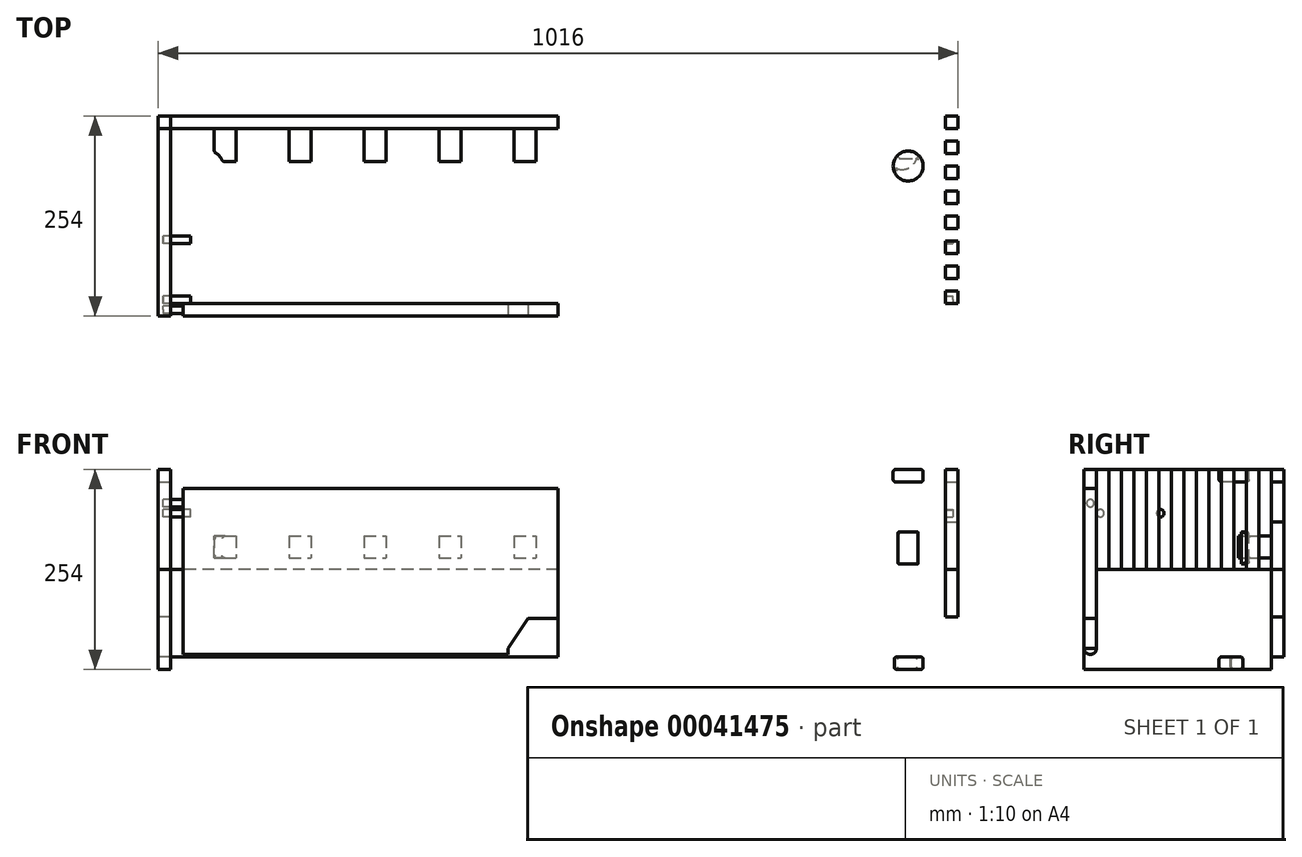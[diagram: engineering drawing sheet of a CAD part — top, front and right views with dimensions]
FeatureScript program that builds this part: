
annotation { "Feature Type Name" : "Feature", "Feature Type Description" : "" }
export const myFeature = defineFeature(function(context is Context, id is Id, definition is map)
    precondition{}
    {
        {
            var Q0;
            Q0=qCreatedBy(makeId("Top.planeOp"),FACE);
            var sketch = newSketch(context, id + "F0", { "sketchPlane" : qUnion([Q0])});
            skLineSegment(sketch, "E0.bottom", {"start": v(-508, 127) * mm, "end": v(0, 127) * mm});
            skLineSegment(sketch, "E0.top", {"start": v(-508, -127) * mm, "end": v(0, -127) * mm});
            skLineSegment(sketch, "E0.left", {"start": v(-508, 127) * mm, "end": v(-508, -127) * mm});
            skLineSegment(sketch, "E0.right", {"start": v(0, 127) * mm, "end": v(0, -127) * mm});
            skLineSegment(sketch, "E1.bottom", {"start": v(-508, 127) * mm, "end": v(-492.13, 127) * mm});
            skLineSegment(sketch, "E1.top", {"start": v(-508, 111.12) * mm, "end": v(-492.13, 111.12) * mm});
            skLineSegment(sketch, "E1.left", {"start": v(-508, 127) * mm, "end": v(-508, 111.12) * mm});
            skLineSegment(sketch, "E1.right", {"start": v(-492.13, 127) * mm, "end": v(-492.13, 111.12) * mm});
            skLineSegment(sketch, "E2.0.1.0", {"start": v(-508, 95.25) * mm, "end": v(-508, 79.37) * mm});
            skLineSegment(sketch, "E2.0.1.1", {"start": v(-508, 95.25) * mm, "end": v(-492.13, 95.25) * mm});
            skLineSegment(sketch, "E2.0.1.2", {"start": v(-492.13, 95.25) * mm, "end": v(-492.13, 79.37) * mm});
            skLineSegment(sketch, "E2.0.1.3", {"start": v(-508, 79.37) * mm, "end": v(-492.13, 79.37) * mm});
            skLineSegment(sketch, "E2.0.2.0", {"start": v(-508, 63.5) * mm, "end": v(-508, 47.62) * mm});
            skLineSegment(sketch, "E2.0.2.1", {"start": v(-508, 63.5) * mm, "end": v(-492.13, 63.5) * mm});
            skLineSegment(sketch, "E2.0.2.2", {"start": v(-492.13, 63.5) * mm, "end": v(-492.13, 47.62) * mm});
            skLineSegment(sketch, "E2.0.2.3", {"start": v(-508, 47.62) * mm, "end": v(-492.13, 47.62) * mm});
            skLineSegment(sketch, "E2.0.3.0", {"start": v(-508, 31.75) * mm, "end": v(-508, 15.87) * mm});
            skLineSegment(sketch, "E2.0.3.1", {"start": v(-508, 31.75) * mm, "end": v(-492.13, 31.75) * mm});
            skLineSegment(sketch, "E2.0.3.2", {"start": v(-492.13, 31.75) * mm, "end": v(-492.13, 15.88) * mm});
            skLineSegment(sketch, "E2.0.3.3", {"start": v(-508, 15.87) * mm, "end": v(-492.13, 15.87) * mm});
            skLineSegment(sketch, "E2.0.4.0", {"start": v(-508, 0) * mm, "end": v(-508, -15.88) * mm});
            skLineSegment(sketch, "E2.0.4.1", {"start": v(-508, 0) * mm, "end": v(-492.13, 0) * mm});
            skLineSegment(sketch, "E2.0.4.2", {"start": v(-492.13, 0) * mm, "end": v(-492.13, -15.87) * mm});
            skLineSegment(sketch, "E2.0.4.3", {"start": v(-508, -15.88) * mm, "end": v(-492.13, -15.88) * mm});
            skLineSegment(sketch, "E2.0.5.0", {"start": v(-508, -31.75) * mm, "end": v(-508, -47.62) * mm});
            skLineSegment(sketch, "E2.0.5.1", {"start": v(-508, -31.75) * mm, "end": v(-492.13, -31.75) * mm});
            skLineSegment(sketch, "E2.0.5.2", {"start": v(-492.13, -31.75) * mm, "end": v(-492.13, -47.62) * mm});
            skLineSegment(sketch, "E2.0.5.3", {"start": v(-508, -47.63) * mm, "end": v(-492.13, -47.63) * mm});
            skLineSegment(sketch, "E2.0.6.0", {"start": v(-508, -63.5) * mm, "end": v(-508, -79.37) * mm});
            skLineSegment(sketch, "E2.0.6.1", {"start": v(-508, -63.5) * mm, "end": v(-492.13, -63.5) * mm});
            skLineSegment(sketch, "E2.0.6.2", {"start": v(-492.13, -63.5) * mm, "end": v(-492.13, -79.37) * mm});
            skLineSegment(sketch, "E2.0.6.3", {"start": v(-508, -79.38) * mm, "end": v(-492.13, -79.38) * mm});
            skLineSegment(sketch, "E2.0.7.0", {"start": v(-508, -95.25) * mm, "end": v(-508, -111.12) * mm});
            skLineSegment(sketch, "E2.0.7.1", {"start": v(-508, -95.25) * mm, "end": v(-492.13, -95.25) * mm});
            skLineSegment(sketch, "E2.0.7.2", {"start": v(-492.13, -95.25) * mm, "end": v(-492.13, -111.12) * mm});
            skLineSegment(sketch, "E2.0.7.3", {"start": v(-508, -111.13) * mm, "end": v(-492.13, -111.13) * mm});
            skLineSegment(sketch, "E2.direction1", {"start": v(-508, 111.12) * mm, "end": v(-482.6, 111.12) * mm, "construction": true});
            skLineSegment(sketch, "E2.direction2", {"start": v(-508, 111.12) * mm, "end": v(-508, 79.37) * mm, "construction": true});
            skLineSegment(sketch, "E3.MirrorCS", {"start": v(508, 127) * mm, "end": v(508, 111.13) * mm});
            skLineSegment(sketch, "E4.MirrorCS", {"start": v(508, 111.13) * mm, "end": v(492.12, 111.13) * mm});
            skLineSegment(sketch, "E5.MirrorCS", {"start": v(508, 111.13) * mm, "end": v(482.6, 111.13) * mm});
            skLineSegment(sketch, "E6.MirrorCS", {"start": v(508, 111.13) * mm, "end": v(508, 79.38) * mm});
            skLineSegment(sketch, "E7.MirrorCS", {"start": v(492.13, -31.75) * mm, "end": v(492.13, -47.62) * mm});
            skLineSegment(sketch, "E8.MirrorCS", {"start": v(508, 15.88) * mm, "end": v(492.13, 15.88) * mm});
            skLineSegment(sketch, "E9.MirrorCS", {"start": v(508, 127) * mm, "end": v(492.12, 127) * mm});
            skLineSegment(sketch, "E10.MirrorCS", {"start": v(508, 63.5) * mm, "end": v(492.12, 63.5) * mm});
            skLineSegment(sketch, "E11.MirrorCS", {"start": v(492.12, 63.5) * mm, "end": v(492.12, 47.63) * mm});
            skLineSegment(sketch, "E12.MirrorCS", {"start": v(492.12, 127) * mm, "end": v(492.12, 111.13) * mm});
            skLineSegment(sketch, "E13.MirrorCS", {"start": v(508, 95.25) * mm, "end": v(508, 79.38) * mm});
            skLineSegment(sketch, "E14.MirrorCS", {"start": v(508, 95.25) * mm, "end": v(492.12, 95.25) * mm});
            skLineSegment(sketch, "E15.MirrorCS", {"start": v(492.12, 95.25) * mm, "end": v(492.12, 79.38) * mm});
            skLineSegment(sketch, "E16.MirrorCS", {"start": v(508, 79.38) * mm, "end": v(492.12, 79.38) * mm});
            skLineSegment(sketch, "E17.MirrorCS", {"start": v(508, 63.5) * mm, "end": v(508, 47.63) * mm});
            skLineSegment(sketch, "E18.MirrorCS", {"start": v(508, -47.62) * mm, "end": v(492.13, -47.62) * mm});
            skLineSegment(sketch, "E19.MirrorCS", {"start": v(508, -15.87) * mm, "end": v(492.13, -15.87) * mm});
            skLineSegment(sketch, "E20.MirrorCS", {"start": v(508, 0) * mm, "end": v(508, -15.87) * mm});
            skLineSegment(sketch, "E21.MirrorCS", {"start": v(508, -63.5) * mm, "end": v(492.13, -63.5) * mm});
            skLineSegment(sketch, "E22.MirrorCS", {"start": v(508, 31.75) * mm, "end": v(508, 15.88) * mm});
            skLineSegment(sketch, "E23.MirrorCS", {"start": v(508, -95.25) * mm, "end": v(508, -111.12) * mm});
            skLineSegment(sketch, "E24.MirrorCS", {"start": v(492.13, -95.25) * mm, "end": v(492.13, -111.12) * mm});
            skLineSegment(sketch, "E25.MirrorCS", {"start": v(508, 0) * mm, "end": v(492.13, 0) * mm});
            skLineSegment(sketch, "E26.MirrorCS", {"start": v(492.13, -63.5) * mm, "end": v(492.13, -79.37) * mm});
            skLineSegment(sketch, "E27.MirrorCS", {"start": v(508, 31.75) * mm, "end": v(492.13, 31.75) * mm});
            skLineSegment(sketch, "E28.MirrorCS", {"start": v(508, -95.25) * mm, "end": v(492.13, -95.25) * mm});
            skLineSegment(sketch, "E29.MirrorCS", {"start": v(508, -31.75) * mm, "end": v(492.13, -31.75) * mm});
            skLineSegment(sketch, "E30.MirrorCS", {"start": v(492.13, 0) * mm, "end": v(492.13, -15.87) * mm});
            skLineSegment(sketch, "E31.MirrorCS", {"start": v(508, -79.37) * mm, "end": v(492.13, -79.37) * mm});
            skLineSegment(sketch, "E32.MirrorCS", {"start": v(492.13, 31.75) * mm, "end": v(492.13, 15.88) * mm});
            skLineSegment(sketch, "E33.MirrorCS", {"start": v(508, -111.12) * mm, "end": v(492.13, -111.12) * mm});
            skLineSegment(sketch, "E34.MirrorCS", {"start": v(508, 127) * mm, "end": v(508, -127) * mm});
            skLineSegment(sketch, "E35.MirrorCS", {"start": v(508, 47.63) * mm, "end": v(492.13, 47.63) * mm});
            skLineSegment(sketch, "E36.MirrorCS", {"start": v(508, -63.5) * mm, "end": v(508, -79.37) * mm});
            skLineSegment(sketch, "E37.MirrorCS", {"start": v(508, -31.75) * mm, "end": v(508, -47.62) * mm});
            skLineSegment(sketch, "E38.MirrorCS", {"start": v(508, 127) * mm, "end": v(0, 127) * mm});
            skLineSegment(sketch, "E39.MirrorCS", {"start": v(508, -127) * mm, "end": v(0, -127) * mm});
            skSolve(sketch);
        }
        {
            var Q0;
            Q0=makeQuery(id+"F0.imprint","IMPRINT",FACE,{"disambiguationData":[TD([[makeQuery(id+"F0.imprint","IMPRINT",EDGE,{"derivedFrom":sQuery(id+"F0.wireOp",EDGE,"E0.bottom")}),-1.0]])]});
            var Q1;
            {var subQ2=sQuery(id+"F0.wireOp",EDGE,"E0.right");Q1=makeQuery(id+"F0.imprint","IMPRINT",FACE,{"disambiguationData":[TD([[makeQuery(id+"F0.imprint","IMPRINT",EDGE,{"derivedFrom":subQ2}),1.0]])]});}
            extrude(context, id + "F1", {"entities" : qUnion([Q0, Q1]), "oppositeDirection" : true, "depth" : 15.88 * mm});
        }
        {
            var Q0;
            {var subQ0=sQuery(id+"F0.wireOp",EDGE,"E0.left");Q0=makeQuery(id+"F1.opExtrude","SWEPT_FACE",FACE,{"disambiguationData":[OSD([subQ0]),TDD([makeQuery(id+"F0.imprint","IMPRINT",EDGE,{"disambiguationData":[TD([[makeQuery(id+"F0.imprint","INTERSECT",VERTEX,{"derivedFrom":[subQ0,sQuery(id+"F0.wireOp",EDGE,"E1.top"),sQuery(id+"F0.wireOp",EDGE,"E1.left")]}),-1.0]])],"derivedFrom":subQ0})])]});}
            var sketch = newSketch(context, id + "F2", { "sketchPlane" : qUnion([Q0])});
            skLineSegment(sketch, "E40.bottom", {"start": v(-127, 0) * mm, "end": v(127, 0) * mm});
            skLineSegment(sketch, "E40.top", {"start": v(-127, -127) * mm, "end": v(127, -127) * mm});
            skLineSegment(sketch, "E40.left", {"start": v(-127, 0) * mm, "end": v(-127, -127) * mm});
            skLineSegment(sketch, "E40.right", {"start": v(127, 0) * mm, "end": v(127, -127) * mm});
            skSolve(sketch);
        }
        {
            var Q0;
            Q0=makeQuery(id+"F2.imprint","IMPRINT",FACE,{"disambiguationData":[TD([[makeQuery(id+"F2.imprint","IMPRINT",EDGE,{"derivedFrom":sQuery(id+"F2.wireOp",EDGE,"E40.top")}),1.0]])]});
            extrude(context, id + "F3", {"entities" : qUnion([Q0]), "oppositeDirection" : true, "depth" : 15.88 * mm});
        }
        {
            var Q0;
            Q0=makeQuery(id+"F1.opExtrude","SWEPT_BODY",BODY,{"disambiguationData":[OSD([sQuery(id+"F0.wireOp",EDGE,"E0.bottom"),sQuery(id+"F0.wireOp",EDGE,"E0.top"),sQuery(id+"F0.wireOp",EDGE,"E0.left"),sQuery(id+"F0.wireOp",EDGE,"E1.top"),sQuery(id+"F0.wireOp",EDGE,"E1.right"),sQuery(id+"F0.wireOp",EDGE,"E2.0.1.1"),sQuery(id+"F0.wireOp",EDGE,"E2.0.1.2"),sQuery(id+"F0.wireOp",EDGE,"E2.0.1.3"),sQuery(id+"F0.wireOp",EDGE,"E2.0.2.1"),sQuery(id+"F0.wireOp",EDGE,"E2.0.2.2"),sQuery(id+"F0.wireOp",EDGE,"E2.0.2.3"),sQuery(id+"F0.wireOp",EDGE,"E2.0.3.1"),sQuery(id+"F0.wireOp",EDGE,"E2.0.3.2"),sQuery(id+"F0.wireOp",EDGE,"E2.0.3.3"),sQuery(id+"F0.wireOp",EDGE,"E2.0.4.1"),sQuery(id+"F0.wireOp",EDGE,"E2.0.4.2"),sQuery(id+"F0.wireOp",EDGE,"E2.0.4.3"),sQuery(id+"F0.wireOp",EDGE,"E2.0.5.1"),sQuery(id+"F0.wireOp",EDGE,"E2.0.5.2"),sQuery(id+"F0.wireOp",EDGE,"E2.0.5.3"),sQuery(id+"F0.wireOp",EDGE,"E2.0.6.1"),sQuery(id+"F0.wireOp",EDGE,"E2.0.6.2"),sQuery(id+"F0.wireOp",EDGE,"E2.0.6.3"),sQuery(id+"F0.wireOp",EDGE,"E2.0.7.1"),sQuery(id+"F0.wireOp",EDGE,"E2.0.7.2"),sQuery(id+"F0.wireOp",EDGE,"E2.0.7.3"),sQuery(id+"F0.wireOp",EDGE,"E5.MirrorCS"),sQuery(id+"F0.wireOp",EDGE,"E7.MirrorCS"),sQuery(id+"F0.wireOp",EDGE,"E8.MirrorCS"),sQuery(id+"F0.wireOp",EDGE,"E10.MirrorCS"),sQuery(id+"F0.wireOp",EDGE,"E11.MirrorCS"),sQuery(id+"F0.wireOp",EDGE,"E12.MirrorCS"),sQuery(id+"F0.wireOp",EDGE,"E14.MirrorCS"),sQuery(id+"F0.wireOp",EDGE,"E15.MirrorCS"),sQuery(id+"F0.wireOp",EDGE,"E16.MirrorCS"),sQuery(id+"F0.wireOp",EDGE,"E18.MirrorCS"),sQuery(id+"F0.wireOp",EDGE,"E19.MirrorCS"),sQuery(id+"F0.wireOp",EDGE,"E21.MirrorCS"),sQuery(id+"F0.wireOp",EDGE,"E24.MirrorCS"),sQuery(id+"F0.wireOp",EDGE,"E25.MirrorCS"),sQuery(id+"F0.wireOp",EDGE,"E26.MirrorCS"),sQuery(id+"F0.wireOp",EDGE,"E27.MirrorCS"),sQuery(id+"F0.wireOp",EDGE,"E28.MirrorCS"),sQuery(id+"F0.wireOp",EDGE,"E29.MirrorCS"),sQuery(id+"F0.wireOp",EDGE,"E30.MirrorCS"),sQuery(id+"F0.wireOp",EDGE,"E31.MirrorCS"),sQuery(id+"F0.wireOp",EDGE,"E32.MirrorCS"),sQuery(id+"F0.wireOp",EDGE,"E33.MirrorCS"),sQuery(id+"F0.wireOp",EDGE,"E34.MirrorCS"),sQuery(id+"F0.wireOp",EDGE,"E35.MirrorCS"),sQuery(id+"F0.wireOp",EDGE,"E38.MirrorCS"),sQuery(id+"F0.wireOp",EDGE,"E39.MirrorCS")])]});
            var Q1;
            Q1=makeQuery(id+"F3.opExtrude","SWEPT_BODY",BODY,{"disambiguationData":[OSD([sQuery(id+"F0.wireOp",EDGE,"E0.left"),sQuery(id+"F0.wireOp",EDGE,"E1.top"),sQuery(id+"F0.wireOp",EDGE,"E1.left"),sQuery(id+"F0.wireOp",EDGE,"E2.0.1.0"),sQuery(id+"F0.wireOp",EDGE,"E2.0.1.1"),sQuery(id+"F2.wireOp",EDGE,"E40.bottom"),sQuery(id+"F2.wireOp",EDGE,"E40.top"),sQuery(id+"F2.wireOp",EDGE,"E40.left"),sQuery(id+"F2.wireOp",EDGE,"E40.right")])]});
            booleanBodies(context, id + "F4", {"operationType" : BooleanOperationType.SUBTRACTION, "tools" : qUnion([Q0]), "targets" : qUnion([Q1]), "keepTools" : true});
        }
        {
            var Q0;
            Q0=makeQuery(id+"F3.opExtrude","SWEPT_FACE",FACE,{"disambiguationData":[OSD([sQuery(id+"F2.wireOp",EDGE,"E40.top")])]});
            cPlane(context, id + "F5", {"entities" : qUnion([Q0]), "cplaneType" : CPlaneType.OFFSET, "offset" : 0 * mm, "width" : 152.4 * mm, "height" : 152.4 * mm});
        }
        {
            var Q0;
            Q0=makeQuery(id+"F3.opExtrude","SWEPT_BODY",BODY,{"disambiguationData":[OSD([sQuery(id+"F0.wireOp",EDGE,"E0.left"),sQuery(id+"F0.wireOp",EDGE,"E1.top"),sQuery(id+"F0.wireOp",EDGE,"E1.left"),sQuery(id+"F0.wireOp",EDGE,"E2.0.1.0"),sQuery(id+"F0.wireOp",EDGE,"E2.0.1.1"),sQuery(id+"F2.wireOp",EDGE,"E40.bottom"),sQuery(id+"F2.wireOp",EDGE,"E40.top"),sQuery(id+"F2.wireOp",EDGE,"E40.left"),sQuery(id+"F2.wireOp",EDGE,"E40.right")])]});
            var Q1;
            Q1=qCreatedBy(id+"F5.planeOp",FACE);
            mirror(context, id + "F6", {"entities" : qUnion([Q0]), "mirrorPlane" : qUnion([Q1])});
        }
        {
            var Q0;
            Q0=makeQuery(id+"F3.opExtrude","CAP_FACE",FACE,{"disambiguationData":[OSD([sQuery(id+"F0.wireOp",EDGE,"E0.left"),sQuery(id+"F0.wireOp",EDGE,"E1.top"),sQuery(id+"F0.wireOp",EDGE,"E1.left"),sQuery(id+"F0.wireOp",EDGE,"E2.0.1.0"),sQuery(id+"F0.wireOp",EDGE,"E2.0.1.1"),sQuery(id+"F2.wireOp",EDGE,"E40.bottom"),sQuery(id+"F2.wireOp",EDGE,"E40.top"),sQuery(id+"F2.wireOp",EDGE,"E40.left"),sQuery(id+"F2.wireOp",EDGE,"E40.right")])],"isStart":false});
            var sketch = newSketch(context, id + "F7", { "sketchPlane" : qUnion([Q0])});
            skLineSegment(sketch, "E41.bottom", {"start": v(-127, -23.81) * mm, "end": v(-111.12, -23.81) * mm});
            skLineSegment(sketch, "E41.top", {"start": v(-118.77, -234.95) * mm, "end": v(-118.77, -234.95) * mm});
            skLineSegment(sketch, "E41.left", {"start": v(-127, -23.81) * mm, "end": v(-127, -227.01) * mm});
            skLineSegment(sketch, "E41.right", {"start": v(-111.12, -23.81) * mm, "end": v(-111.12, -227.01) * mm});
            skCircle(sketch, "E42", {"center": v(-119.06, -42.86) * mm, "radius": 20.64 * mm, "construction": true});
            skPoint(sketch, "E42.centerSnap0", {"position": v(-119.06, -23.81) * mm});
            skPoint(sketch, "E43", {"position": v(-119.06, -22.23) * mm});
            skCircle(sketch, "E44", {"center": v(-119.06, -42.86) * mm, "radius": 7.94 * mm, "construction": true});
            skPoint(sketch, "E45", {"position": v(-119.06, -50.8) * mm});
            skLineSegment(sketch, "E46", {"start": v(-119.06, -50.8) * mm, "end": v(-30.16, -50.8) * mm, "construction": true});
            skPoint(sketch, "E47", {"position": v(-30.16, -55.56) * mm});
            skCircle(sketch, "E48", {"center": v(-119.06, -42.86) * mm, "radius": 4.76 * mm});
            skCircle(sketch, "E49", {"center": v(-30.16, -55.56) * mm, "radius": 4.76 * mm});
            skPoint(sketch, "E50", {"position": v(-106.36, -55.56) * mm});
            skCircle(sketch, "E51", {"center": v(-106.36, -55.56) * mm, "radius": 4.76 * mm});
            skPoint(sketch, "E52.visualSharp", {"position": v(-127, -234.95) * mm});
            skArc(sketch, "E52.filletArc", {"start": v(-127, -227.01) * mm, "mid": v(-124.68, -232.63) * mm, "end": v(-119.06, -234.95) * mm});
            skPoint(sketch, "E53.visualSharp", {"position": v(-111.12, -234.95) * mm});
            skArc(sketch, "E53.filletArc", {"start": v(-119.06, -234.95) * mm, "mid": v(-113.45, -232.63) * mm, "end": v(-111.12, -227.01) * mm});
            skLineSegment(sketch, "E54.bottom", {"start": v(-123.82, -42.86) * mm, "end": v(-114.3, -42.86) * mm});
            skLineSegment(sketch, "E54.top", {"start": v(-123.82, -195.26) * mm, "end": v(-114.3, -195.26) * mm});
            skLineSegment(sketch, "E54.left", {"start": v(-123.82, -42.86) * mm, "end": v(-123.82, -195.26) * mm});
            skLineSegment(sketch, "E54.right", {"start": v(-114.3, -42.86) * mm, "end": v(-114.3, -195.26) * mm});
            skSolve(sketch);
        }
        {
            var Q0;
            Q0=makeQuery(id+"F7.imprint","IMPRINT",FACE,{"disambiguationData":[TD([[makeQuery(id+"F7.imprint","IMPRINT",EDGE,{"derivedFrom":sQuery(id+"F7.wireOp",EDGE,"E51")}),1.0]])]});
            var Q1;
            Q1=makeQuery(id+"F7.imprint","IMPRINT",FACE,{"disambiguationData":[TD([[makeQuery(id+"F7.imprint","IMPRINT",EDGE,{"derivedFrom":sQuery(id+"F7.wireOp",EDGE,"E48")}),1.0]])]});
            var Q2;
            Q2=makeQuery(id+"F7.imprint","IMPRINT",FACE,{"disambiguationData":[TD([[makeQuery(id+"F7.imprint","IMPRINT",EDGE,{"derivedFrom":sQuery(id+"F7.wireOp",EDGE,"E49")}),1.0]])]});
            extrude(context, id + "F8", {"entities" : qUnion([Q0, Q1, Q2]), "depth" : 25.4 * mm, "hasSecondDirection" : true, "secondDirectionOppositeDirection" : true, "secondDirectionDepth" : 9.52 * mm});
        }
        {
            var Q0;
            Q0=makeQuery(id+"F1.opExtrude","SWEPT_FACE",FACE,{"disambiguationData":[OSD([sQuery(id+"F0.wireOp",EDGE,"E0.bottom"),sQuery(id+"F0.wireOp",EDGE,"E38.MirrorCS")])]});
            var sketch = newSketch(context, id + "F9", { "sketchPlane" : qUnion([Q0])});
            skLineSegment(sketch, "E55", {"start": v(0, -15.88) * mm, "end": v(492.13, -15.88) * mm});
            skLineSegment(sketch, "E56", {"start": v(492.13, -15.88) * mm, "end": v(492.13, -66.67) * mm});
            skLineSegment(sketch, "E57", {"start": v(492.12, -66.68) * mm, "end": v(508, -66.68) * mm});
            skLineSegment(sketch, "E58", {"start": v(508, -66.68) * mm, "end": v(508, -127) * mm});
            skLineSegment(sketch, "E59", {"start": v(0, -15.88) * mm, "end": v(0, -127) * mm});
            skLineSegment(sketch, "E60", {"start": v(0, -127) * mm, "end": v(508, -127) * mm});
            skLineSegment(sketch, "E61.MirrorCS", {"start": v(0, -238.13) * mm, "end": v(0, -127) * mm});
            skLineSegment(sketch, "E62.MirrorCS", {"start": v(0, -238.13) * mm, "end": v(492.13, -238.13) * mm});
            skLineSegment(sketch, "E63.MirrorCS", {"start": v(492.13, -238.13) * mm, "end": v(492.13, -187.33) * mm});
            skLineSegment(sketch, "E64.MirrorCS", {"start": v(492.12, -187.33) * mm, "end": v(508, -187.33) * mm});
            skLineSegment(sketch, "E65.MirrorCS", {"start": v(508, -187.33) * mm, "end": v(508, -127) * mm});
            skLineSegment(sketch, "E66.MirrorCS", {"start": v(0, -15.88) * mm, "end": v(-492.13, -15.88) * mm});
            skLineSegment(sketch, "E67.MirrorCS", {"start": v(-492.13, -15.88) * mm, "end": v(-492.13, -66.67) * mm});
            skLineSegment(sketch, "E68.MirrorCS", {"start": v(-492.12, -187.33) * mm, "end": v(-508, -187.33) * mm});
            skLineSegment(sketch, "E69.MirrorCS", {"start": v(-492.12, -66.68) * mm, "end": v(-508, -66.68) * mm});
            skLineSegment(sketch, "E70.MirrorCS", {"start": v(-508, -187.33) * mm, "end": v(-508, -127) * mm});
            skLineSegment(sketch, "E71.MirrorCS", {"start": v(-508, -66.67) * mm, "end": v(-508, -127) * mm});
            skLineSegment(sketch, "E72.MirrorCS", {"start": v(0, -238.13) * mm, "end": v(-492.13, -238.13) * mm});
            skLineSegment(sketch, "E73.MirrorCS", {"start": v(-492.13, -238.13) * mm, "end": v(-492.13, -187.33) * mm});
            skSolve(sketch);
        }
        {
            var Q0;
            Q0=makeQuery(id+"F9.imprint","IMPRINT",FACE,{"disambiguationData":[TD([[makeQuery(id+"F9.imprint","IMPRINT",EDGE,{"derivedFrom":sQuery(id+"F9.wireOp",EDGE,"E59")}),-1.0]])]});
            var Q1;
            Q1=makeQuery(id+"F9.imprint","IMPRINT",FACE,{"disambiguationData":[TD([[makeQuery(id+"F9.imprint","IMPRINT",EDGE,{"derivedFrom":sQuery(id+"F9.wireOp",EDGE,"E60")}),-1.0]])]});
            var Q2;
            Q2=makeQuery(id+"F9.imprint","IMPRINT",FACE,{"disambiguationData":[TD([[makeQuery(id+"F9.imprint","IMPRINT",EDGE,{"derivedFrom":sQuery(id+"F9.wireOp",EDGE,"E55")}),1.0]])]});
            extrude(context, id + "F10", {"entities" : qUnion([Q0, Q1, Q2]), "oppositeDirection" : true, "depth" : 15.88 * mm});
        }
        {
            var Q0;
            Q0=makeQuery(id+"F10.opExtrude","SWEPT_BODY",BODY,{"disambiguationData":[OSD([sQuery(id+"F9.wireOp",EDGE,"E55"),sQuery(id+"F9.wireOp",EDGE,"E56"),sQuery(id+"F9.wireOp",EDGE,"E57"),sQuery(id+"F9.wireOp",EDGE,"E58"),sQuery(id+"F9.wireOp",EDGE,"E62.MirrorCS"),sQuery(id+"F9.wireOp",EDGE,"E63.MirrorCS"),sQuery(id+"F9.wireOp",EDGE,"E64.MirrorCS"),sQuery(id+"F9.wireOp",EDGE,"E65.MirrorCS"),sQuery(id+"F9.wireOp",EDGE,"E66.MirrorCS"),sQuery(id+"F9.wireOp",EDGE,"E67.MirrorCS"),sQuery(id+"F9.wireOp",EDGE,"E68.MirrorCS"),sQuery(id+"F9.wireOp",EDGE,"E69.MirrorCS"),sQuery(id+"F9.wireOp",EDGE,"E70.MirrorCS"),sQuery(id+"F9.wireOp",EDGE,"E71.MirrorCS"),sQuery(id+"F9.wireOp",EDGE,"E72.MirrorCS"),sQuery(id+"F9.wireOp",EDGE,"E73.MirrorCS")])]});
            var Q1;
            Q1=makeQuery(id+"F3.opExtrude","SWEPT_BODY",BODY,{"disambiguationData":[OSD([sQuery(id+"F0.wireOp",EDGE,"E0.left"),sQuery(id+"F0.wireOp",EDGE,"E1.top"),sQuery(id+"F0.wireOp",EDGE,"E1.left"),sQuery(id+"F0.wireOp",EDGE,"E2.0.1.0"),sQuery(id+"F0.wireOp",EDGE,"E2.0.1.1"),sQuery(id+"F2.wireOp",EDGE,"E40.bottom"),sQuery(id+"F2.wireOp",EDGE,"E40.top"),sQuery(id+"F2.wireOp",EDGE,"E40.left"),sQuery(id+"F2.wireOp",EDGE,"E40.right")])]});
            booleanBodies(context, id + "F11", {"operationType" : BooleanOperationType.SUBTRACTION, "tools" : qUnion([Q0]), "targets" : qUnion([Q1]), "keepTools" : true});
        }
        {
            var Q0;
            Q0=makeQuery(id+"F3.opExtrude","SWEPT_BODY",BODY,{"disambiguationData":[OSD([sQuery(id+"F0.wireOp",EDGE,"E0.left"),sQuery(id+"F0.wireOp",EDGE,"E1.top"),sQuery(id+"F0.wireOp",EDGE,"E1.left"),sQuery(id+"F0.wireOp",EDGE,"E2.0.1.0"),sQuery(id+"F0.wireOp",EDGE,"E2.0.1.1"),sQuery(id+"F2.wireOp",EDGE,"E40.bottom"),sQuery(id+"F2.wireOp",EDGE,"E40.top"),sQuery(id+"F2.wireOp",EDGE,"E40.left"),sQuery(id+"F2.wireOp",EDGE,"E40.right")])]});
            var Q1;
            Q1=makeQuery(id+"F8.opExtrude","SWEPT_BODY",BODY,{"disambiguationData":[OSD([sQuery(id+"F7.wireOp",EDGE,"E48")])]});
            var Q2;
            Q2=makeQuery(id+"F8.opExtrude","SWEPT_BODY",BODY,{"disambiguationData":[OSD([sQuery(id+"F7.wireOp",EDGE,"E51")])]});
            var Q3;
            Q3=makeQuery(id+"F8.opExtrude","SWEPT_BODY",BODY,{"disambiguationData":[OSD([sQuery(id+"F7.wireOp",EDGE,"E49")])]});
            var Q4;
            Q4=qCreatedBy(makeId("Right.planeOp"),FACE);
            mirror(context, id + "F12", {"entities" : qUnion([Q0, Q1, Q2, Q3]), "mirrorPlane" : qUnion([Q4])});
        }
        {
            var Q0;
            Q0=makeQuery(id+"F1.opExtrude","SWEPT_BODY",BODY,{"disambiguationData":[OSD([sQuery(id+"F0.wireOp",EDGE,"E0.bottom"),sQuery(id+"F0.wireOp",EDGE,"E0.top"),sQuery(id+"F0.wireOp",EDGE,"E0.left"),sQuery(id+"F0.wireOp",EDGE,"E1.top"),sQuery(id+"F0.wireOp",EDGE,"E1.right"),sQuery(id+"F0.wireOp",EDGE,"E2.0.1.1"),sQuery(id+"F0.wireOp",EDGE,"E2.0.1.2"),sQuery(id+"F0.wireOp",EDGE,"E2.0.1.3"),sQuery(id+"F0.wireOp",EDGE,"E2.0.2.1"),sQuery(id+"F0.wireOp",EDGE,"E2.0.2.2"),sQuery(id+"F0.wireOp",EDGE,"E2.0.2.3"),sQuery(id+"F0.wireOp",EDGE,"E2.0.3.1"),sQuery(id+"F0.wireOp",EDGE,"E2.0.3.2"),sQuery(id+"F0.wireOp",EDGE,"E2.0.3.3"),sQuery(id+"F0.wireOp",EDGE,"E2.0.4.1"),sQuery(id+"F0.wireOp",EDGE,"E2.0.4.2"),sQuery(id+"F0.wireOp",EDGE,"E2.0.4.3"),sQuery(id+"F0.wireOp",EDGE,"E2.0.5.1"),sQuery(id+"F0.wireOp",EDGE,"E2.0.5.2"),sQuery(id+"F0.wireOp",EDGE,"E2.0.5.3"),sQuery(id+"F0.wireOp",EDGE,"E2.0.6.1"),sQuery(id+"F0.wireOp",EDGE,"E2.0.6.2"),sQuery(id+"F0.wireOp",EDGE,"E2.0.6.3"),sQuery(id+"F0.wireOp",EDGE,"E2.0.7.1"),sQuery(id+"F0.wireOp",EDGE,"E2.0.7.2"),sQuery(id+"F0.wireOp",EDGE,"E2.0.7.3"),sQuery(id+"F0.wireOp",EDGE,"E5.MirrorCS"),sQuery(id+"F0.wireOp",EDGE,"E7.MirrorCS"),sQuery(id+"F0.wireOp",EDGE,"E8.MirrorCS"),sQuery(id+"F0.wireOp",EDGE,"E10.MirrorCS"),sQuery(id+"F0.wireOp",EDGE,"E11.MirrorCS"),sQuery(id+"F0.wireOp",EDGE,"E12.MirrorCS"),sQuery(id+"F0.wireOp",EDGE,"E14.MirrorCS"),sQuery(id+"F0.wireOp",EDGE,"E15.MirrorCS"),sQuery(id+"F0.wireOp",EDGE,"E16.MirrorCS"),sQuery(id+"F0.wireOp",EDGE,"E18.MirrorCS"),sQuery(id+"F0.wireOp",EDGE,"E19.MirrorCS"),sQuery(id+"F0.wireOp",EDGE,"E21.MirrorCS"),sQuery(id+"F0.wireOp",EDGE,"E24.MirrorCS"),sQuery(id+"F0.wireOp",EDGE,"E25.MirrorCS"),sQuery(id+"F0.wireOp",EDGE,"E26.MirrorCS"),sQuery(id+"F0.wireOp",EDGE,"E27.MirrorCS"),sQuery(id+"F0.wireOp",EDGE,"E28.MirrorCS"),sQuery(id+"F0.wireOp",EDGE,"E29.MirrorCS"),sQuery(id+"F0.wireOp",EDGE,"E30.MirrorCS"),sQuery(id+"F0.wireOp",EDGE,"E31.MirrorCS"),sQuery(id+"F0.wireOp",EDGE,"E32.MirrorCS"),sQuery(id+"F0.wireOp",EDGE,"E33.MirrorCS"),sQuery(id+"F0.wireOp",EDGE,"E34.MirrorCS"),sQuery(id+"F0.wireOp",EDGE,"E35.MirrorCS"),sQuery(id+"F0.wireOp",EDGE,"E38.MirrorCS"),sQuery(id+"F0.wireOp",EDGE,"E39.MirrorCS")])]});
            var Q1;
            Q1=qCreatedBy(id+"F5.planeOp",FACE);
            mirror(context, id + "F13", {"entities" : qUnion([Q0]), "mirrorPlane" : qUnion([Q1])});
        }
        {
            var Q0;
            {var subQ10=sQuery(id+"F7.wireOp",EDGE,"E52.filletArc");Q0=makeQuery(id+"F7.imprint","IMPRINT",FACE,{"disambiguationData":[TD([[makeQuery(id+"F7.imprint","IMPRINT",EDGE,{"derivedFrom":subQ10}),1.0]])]});}
            var Q1;
            {var subQ5=sQuery(id+"F7.wireOp",EDGE,"E54.top");Q1=makeQuery(id+"F7.imprint","IMPRINT",FACE,{"disambiguationData":[TD([[makeQuery(id+"F7.imprint","IMPRINT",EDGE,{"derivedFrom":subQ5}),1.0]])]});}
            var Q2;
            {var subQ13=sQuery(id+"F7.wireOp",EDGE,"E41.bottom");Q2=makeQuery(id+"F7.imprint","IMPRINT",FACE,{"disambiguationData":[TD([[makeQuery(id+"F7.imprint","IMPRINT",EDGE,{"derivedFrom":subQ13}),-1.0]])]});}
            var Q3;
            {var subQ0=makeQuery(id+"F3.opExtrude","CAP_EDGE",EDGE,{"disambiguationData":[OSD([sQuery(id+"F2.wireOp",EDGE,"E40.top")])],"isStart":false});var subQ3=sQuery(id+"F7.wireOp",EDGE,"E54.left");var subQ4=makeQuery(id+"F7.imprint","INTERSECT",VERTEX,{"derivedFrom":[subQ0,subQ3]});Q3=makeQuery(id+"F7.imprint","IMPRINT",FACE,{"disambiguationData":[TD([[makeQuery(id+"F7.imprint","IMPRINT",EDGE,{"disambiguationData":[TD([[subQ4,1.0]])],"derivedFrom":subQ0}),-1.0]])]});}
            var Q4;
            {var subQ0=sQuery(id+"F7.wireOp",EDGE,"E54.bottom");Q4=makeQuery(id+"F7.imprint","IMPRINT",FACE,{"disambiguationData":[TD([[makeQuery(id+"F7.imprint","IMPRINT",EDGE,{"derivedFrom":subQ0}),1.0]])]});}
            var Q5;
            {var subQ0=sQuery(id+"F7.wireOp",EDGE,"E54.bottom");Q5=makeQuery(id+"F7.imprint","IMPRINT",FACE,{"disambiguationData":[TD([[makeQuery(id+"F7.imprint","IMPRINT",EDGE,{"derivedFrom":subQ0}),-1.0]])]});}
            var Q6;
            Q6=qCreatedBy(makeId("Right.planeOp"),FACE);
            var Q7;
            Q7=qCreatedBy(makeId("Right.planeOp"),FACE);
            extrude(context, id + "F14", {"entities" : qUnion([Q0, Q1, Q2, Q3, Q4, Q5]), "endBound" : BoundingType.UP_TO_SURFACE, "endBoundEntityFace" : qUnion([Q6]), "depth" : 50.8 * mm, "hasSecondDirection" : true, "secondDirectionOppositeDirection" : false, "secondDirectionBoundEntityFace" : qUnion([Q7]), "secondDirectionDepth" : 3.17 * mm});
        }
        {
            var Q0;
            Q0=makeQuery(id+"F14.opExtrude","CAP_FACE",FACE,{"disambiguationData":[OSD([sQuery(id+"F7.wireOp",EDGE,"E41.bottom"),sQuery(id+"F7.wireOp",EDGE,"E41.left"),sQuery(id+"F7.wireOp",EDGE,"E41.right"),sQuery(id+"F7.wireOp",EDGE,"E52.filletArc"),sQuery(id+"F7.wireOp",EDGE,"E53.filletArc")])],"isStart":true});
            var sketch = newSketch(context, id + "F15", { "sketchPlane" : qUnion([Q0])});
            skCircle(sketch, "E74.0", {"center": v(119.06, -42.86) * mm, "radius": 4.76 * mm});
            skLineSegment(sketch, "E74.1", {"start": v(114.3, -42.86) * mm, "end": v(114.3, -195.26) * mm});
            skLineSegment(sketch, "E74.2", {"start": v(123.82, -42.86) * mm, "end": v(123.82, -195.26) * mm});
            skLineSegment(sketch, "E74.3", {"start": v(123.82, -195.26) * mm, "end": v(114.3, -195.26) * mm});
            skSolve(sketch);
        }
        {
            var Q0;
            {var subQ1=sQuery(id+"F15.wireOp",EDGE,"E74.1");Q0=makeQuery(id+"F15.imprint","IMPRINT",FACE,{"disambiguationData":[TD([[makeQuery(id+"F15.imprint","IMPRINT",EDGE,{"derivedFrom":subQ1}),1.0]])]});}
            var Q1;
            {var subQ0=sQuery(id+"F15.wireOp",EDGE,"E74.0");var subQ2=makeQuery(id+"F15.imprint","INTERSECT",VERTEX,{"derivedFrom":[subQ0,sQuery(id+"F15.wireOp",EDGE,"E74.1")]});Q1=makeQuery(id+"F15.imprint","IMPRINT",FACE,{"disambiguationData":[TD([[makeQuery(id+"F15.imprint","IMPRINT",EDGE,{"disambiguationData":[TD([[subQ2,1.0]])],"derivedFrom":subQ0}),-1.0]])]});}
            extrude(context, id + "F16", {"entities" : qUnion([Q0, Q1]), "operationType" : NewBodyOperationType.REMOVE, "oppositeDirection" : true, "depth" : 12.7 * mm});
        }
        {
            var Q0;
            Q0=makeQuery(id+"F14.opExtrude","SWEPT_BODY",BODY,{"disambiguationData":[OSD([sQuery(id+"F7.wireOp",EDGE,"E41.bottom"),sQuery(id+"F7.wireOp",EDGE,"E41.left"),sQuery(id+"F7.wireOp",EDGE,"E41.right"),sQuery(id+"F7.wireOp",EDGE,"E52.filletArc"),sQuery(id+"F7.wireOp",EDGE,"E53.filletArc")])]});
            var Q1;
            Q1=qCreatedBy(makeId("Right.planeOp"),FACE);
            mirror(context, id + "F17", {"operationType" : NewBodyOperationType.ADD, "entities" : qUnion([Q0]), "mirrorPlane" : qUnion([Q1])});
        }
        {
            var Q0;
            {var subQ0=makeQuery(id+"F14.opExtrude","SWEPT_FACE",FACE,{"disambiguationData":[OSD([sQuery(id+"F7.wireOp",EDGE,"E41.left")])]});Q0=makeQuery(id+"F17.boolean.opBoolean","MERGE",FACE,{"derivedFrom":[subQ0,makeQuery(id+"F17.opPattern","COPY",FACE,{"derivedFrom":subQ0,"instanceName":"1"})]});}
            var sketch = newSketch(context, id + "F18", { "sketchPlane" : qUnion([Q0])});
            skLineSegment(sketch, "E75", {"start": v(0, -188.91) * mm, "end": v(-38.1, -188.91) * mm});
            skLineSegment(sketch, "E76", {"start": v(-38.1, -188.91) * mm, "end": v(-63.5, -227.01) * mm});
            skLineSegment(sketch, "E77", {"start": v(-63.5, -227.01) * mm, "end": v(-63.5, -238.13) * mm});
            skLineSegment(sketch, "E78", {"start": v(-63.5, -238.13) * mm, "end": v(0, -238.13) * mm});
            skLineSegment(sketch, "E79.MirrorCS", {"start": v(63.5, -238.13) * mm, "end": v(0, -238.13) * mm});
            skLineSegment(sketch, "E80.MirrorCS", {"start": v(63.5, -227.01) * mm, "end": v(63.5, -238.13) * mm});
            skLineSegment(sketch, "E81.MirrorCS", {"start": v(0, -188.91) * mm, "end": v(38.1, -188.91) * mm});
            skLineSegment(sketch, "E82.MirrorCS", {"start": v(38.1, -188.91) * mm, "end": v(63.5, -227.01) * mm});
            skSolve(sketch);
        }
        {
            var Q0;
            Q0=makeQuery(id+"F18.imprint","IMPRINT",FACE,{"disambiguationData":[TD([[makeQuery(id+"F18.imprint","IMPRINT",EDGE,{"derivedFrom":sQuery(id+"F18.wireOp",EDGE,"E75")}),1.0]])]});
            var Q1;
            {var subQ0=sQuery(id+"F18.wireOp",EDGE,"E77");Q1=makeQuery(id+"F18.imprint","IMPRINT",FACE,{"disambiguationData":[TD([[makeQuery(id+"F18.imprint","IMPRINT",EDGE,{"derivedFrom":subQ0}),1.0]])]});}
            extrude(context, id + "F19", {"entities" : qUnion([Q0, Q1]), "operationType" : NewBodyOperationType.REMOVE, "endBound" : BoundingType.UP_TO_NEXT, "oppositeDirection" : true, "depth" : 25.4 * mm});
        }
        {
            var Q0;
            Q0=makeQuery(id+"F10.opExtrude","CAP_FACE",FACE,{"disambiguationData":[OSD([sQuery(id+"F9.wireOp",EDGE,"E55"),sQuery(id+"F9.wireOp",EDGE,"E56"),sQuery(id+"F9.wireOp",EDGE,"E57"),sQuery(id+"F9.wireOp",EDGE,"E58"),sQuery(id+"F9.wireOp",EDGE,"E62.MirrorCS"),sQuery(id+"F9.wireOp",EDGE,"E63.MirrorCS"),sQuery(id+"F9.wireOp",EDGE,"E64.MirrorCS"),sQuery(id+"F9.wireOp",EDGE,"E65.MirrorCS"),sQuery(id+"F9.wireOp",EDGE,"E66.MirrorCS"),sQuery(id+"F9.wireOp",EDGE,"E67.MirrorCS"),sQuery(id+"F9.wireOp",EDGE,"E68.MirrorCS"),sQuery(id+"F9.wireOp",EDGE,"E69.MirrorCS"),sQuery(id+"F9.wireOp",EDGE,"E70.MirrorCS"),sQuery(id+"F9.wireOp",EDGE,"E71.MirrorCS"),sQuery(id+"F9.wireOp",EDGE,"E72.MirrorCS"),sQuery(id+"F9.wireOp",EDGE,"E73.MirrorCS")])],"isStart":false});
            var sketch = newSketch(context, id + "F20", { "sketchPlane" : qUnion([Q0])});
            skLineSegment(sketch, "E83.bottom", {"start": v(-469.9, -79.37) * mm, "end": v(469.9, -79.38) * mm});
            skLineSegment(sketch, "E83.top", {"start": v(-469.9, -120.01) * mm, "end": v(469.9, -120.02) * mm});
            skLineSegment(sketch, "E83.left", {"start": v(-469.9, -79.37) * mm, "end": v(-469.9, -120.01) * mm});
            skLineSegment(sketch, "E83.right", {"start": v(469.9, -79.37) * mm, "end": v(469.9, -120.01) * mm});
            skLineSegment(sketch, "E84.bottom", {"start": v(-436.88, -84.7) * mm, "end": v(-408.94, -84.7) * mm});
            skLineSegment(sketch, "E84.top", {"start": v(-436.88, -112.65) * mm, "end": v(-408.94, -112.65) * mm});
            skLineSegment(sketch, "E84.left", {"start": v(-436.88, -84.7) * mm, "end": v(-436.88, -112.65) * mm});
            skLineSegment(sketch, "E84.right", {"start": v(-408.94, -84.7) * mm, "end": v(-408.94, -112.65) * mm});
            skLineSegment(sketch, "E85.1.0.0", {"start": v(-341.63, -84.7) * mm, "end": v(-313.7, -84.7) * mm});
            skLineSegment(sketch, "E85.1.0.1", {"start": v(-313.7, -84.7) * mm, "end": v(-313.7, -112.65) * mm});
            skLineSegment(sketch, "E85.1.0.2", {"start": v(-341.63, -112.65) * mm, "end": v(-313.7, -112.65) * mm});
            skLineSegment(sketch, "E85.1.0.3", {"start": v(-341.63, -84.7) * mm, "end": v(-341.63, -112.65) * mm});
            skLineSegment(sketch, "E85.2.0.0", {"start": v(-246.38, -84.7) * mm, "end": v(-218.44, -84.7) * mm});
            skLineSegment(sketch, "E85.2.0.1", {"start": v(-218.44, -84.7) * mm, "end": v(-218.44, -112.65) * mm});
            skLineSegment(sketch, "E85.2.0.2", {"start": v(-246.38, -112.65) * mm, "end": v(-218.44, -112.65) * mm});
            skLineSegment(sketch, "E85.2.0.3", {"start": v(-246.38, -84.7) * mm, "end": v(-246.38, -112.65) * mm});
            skLineSegment(sketch, "E85.3.0.0", {"start": v(-151.13, -84.7) * mm, "end": v(-123.2, -84.7) * mm});
            skLineSegment(sketch, "E85.3.0.1", {"start": v(-123.2, -84.7) * mm, "end": v(-123.2, -112.65) * mm});
            skLineSegment(sketch, "E85.3.0.2", {"start": v(-151.13, -112.65) * mm, "end": v(-123.2, -112.65) * mm});
            skLineSegment(sketch, "E85.3.0.3", {"start": v(-151.13, -84.7) * mm, "end": v(-151.13, -112.65) * mm});
            skLineSegment(sketch, "E85.4.0.0", {"start": v(-55.88, -84.7) * mm, "end": v(-27.94, -84.7) * mm});
            skLineSegment(sketch, "E85.4.0.1", {"start": v(-27.94, -84.7) * mm, "end": v(-27.94, -112.65) * mm});
            skLineSegment(sketch, "E85.4.0.2", {"start": v(-55.88, -112.65) * mm, "end": v(-27.94, -112.65) * mm});
            skLineSegment(sketch, "E85.4.0.3", {"start": v(-55.88, -84.7) * mm, "end": v(-55.88, -112.65) * mm});
            skLineSegment(sketch, "E85.5.0.0", {"start": v(39.37, -84.7) * mm, "end": v(67.3, -84.7) * mm});
            skLineSegment(sketch, "E85.5.0.1", {"start": v(67.3, -84.7) * mm, "end": v(67.3, -112.65) * mm});
            skLineSegment(sketch, "E85.5.0.2", {"start": v(39.37, -112.65) * mm, "end": v(67.3, -112.65) * mm});
            skLineSegment(sketch, "E85.5.0.3", {"start": v(39.37, -84.7) * mm, "end": v(39.37, -112.65) * mm});
            skLineSegment(sketch, "E85.6.0.0", {"start": v(134.62, -84.7) * mm, "end": v(162.56, -84.7) * mm});
            skLineSegment(sketch, "E85.6.0.1", {"start": v(162.56, -84.7) * mm, "end": v(162.56, -112.65) * mm});
            skLineSegment(sketch, "E85.6.0.2", {"start": v(134.62, -112.65) * mm, "end": v(162.56, -112.65) * mm});
            skLineSegment(sketch, "E85.6.0.3", {"start": v(134.62, -84.7) * mm, "end": v(134.62, -112.65) * mm});
            skLineSegment(sketch, "E85.7.0.0", {"start": v(229.87, -84.7) * mm, "end": v(257.8, -84.7) * mm});
            skLineSegment(sketch, "E85.7.0.1", {"start": v(257.8, -84.7) * mm, "end": v(257.8, -112.65) * mm});
            skLineSegment(sketch, "E85.7.0.2", {"start": v(229.87, -112.65) * mm, "end": v(257.8, -112.65) * mm});
            skLineSegment(sketch, "E85.7.0.3", {"start": v(229.87, -84.7) * mm, "end": v(229.87, -112.65) * mm});
            skLineSegment(sketch, "E85.8.0.0", {"start": v(325.12, -84.7) * mm, "end": v(353.06, -84.7) * mm});
            skLineSegment(sketch, "E85.8.0.1", {"start": v(353.06, -84.7) * mm, "end": v(353.06, -112.65) * mm});
            skLineSegment(sketch, "E85.8.0.2", {"start": v(325.12, -112.65) * mm, "end": v(353.06, -112.65) * mm});
            skLineSegment(sketch, "E85.8.0.3", {"start": v(325.12, -84.7) * mm, "end": v(325.12, -112.65) * mm});
            skLineSegment(sketch, "E85.direction1", {"start": v(-436.88, -84.7) * mm, "end": v(-341.63, -84.7) * mm, "construction": true});
            skPoint(sketch, "E86", {"position": v(0, -79.38) * mm});
            skSolve(sketch);
        }
        {
            var Q0;
            Q0=makeQuery(id+"F20.imprint","IMPRINT",FACE,{"disambiguationData":[TD([[makeQuery(id+"F20.imprint","IMPRINT",EDGE,{"derivedFrom":sQuery(id+"F20.wireOp",EDGE,"E83.bottom")}),-1.0]])]});
            extrude(context, id + "F21", {"entities" : qUnion([Q0]), "depth" : 38.1 * mm});
        }
        {
            var Q0;
            Q0=makeQuery(id+"F20.imprint","IMPRINT",FACE,{"disambiguationData":[TD([[makeQuery(id+"F20.imprint","IMPRINT",EDGE,{"derivedFrom":sQuery(id+"F20.wireOp",EDGE,"E84.bottom")}),-1.0]])]});
            var Q1;
            Q1=makeQuery(id+"F20.imprint","IMPRINT",FACE,{"disambiguationData":[TD([[makeQuery(id+"F20.imprint","IMPRINT",EDGE,{"derivedFrom":sQuery(id+"F20.wireOp",EDGE,"E85.1.0.0")}),-1.0]])]});
            var Q2;
            Q2=makeQuery(id+"F20.imprint","IMPRINT",FACE,{"disambiguationData":[TD([[makeQuery(id+"F20.imprint","IMPRINT",EDGE,{"derivedFrom":sQuery(id+"F20.wireOp",EDGE,"E85.2.0.0")}),-1.0]])]});
            var Q3;
            Q3=makeQuery(id+"F20.imprint","IMPRINT",FACE,{"disambiguationData":[TD([[makeQuery(id+"F20.imprint","IMPRINT",EDGE,{"derivedFrom":sQuery(id+"F20.wireOp",EDGE,"E85.3.0.0")}),-1.0]])]});
            var Q4;
            Q4=makeQuery(id+"F20.imprint","IMPRINT",FACE,{"disambiguationData":[TD([[makeQuery(id+"F20.imprint","IMPRINT",EDGE,{"derivedFrom":sQuery(id+"F20.wireOp",EDGE,"E85.4.0.0")}),-1.0]])]});
            var Q5;
            Q5=makeQuery(id+"F20.imprint","IMPRINT",FACE,{"disambiguationData":[TD([[makeQuery(id+"F20.imprint","IMPRINT",EDGE,{"derivedFrom":sQuery(id+"F20.wireOp",EDGE,"E85.5.0.0")}),-1.0]])]});
            var Q6;
            Q6=makeQuery(id+"F20.imprint","IMPRINT",FACE,{"disambiguationData":[TD([[makeQuery(id+"F20.imprint","IMPRINT",EDGE,{"derivedFrom":sQuery(id+"F20.wireOp",EDGE,"E85.6.0.0")}),-1.0]])]});
            var Q7;
            Q7=makeQuery(id+"F20.imprint","IMPRINT",FACE,{"disambiguationData":[TD([[makeQuery(id+"F20.imprint","IMPRINT",EDGE,{"derivedFrom":sQuery(id+"F20.wireOp",EDGE,"E85.7.0.0")}),-1.0]])]});
            var Q8;
            Q8=makeQuery(id+"F20.imprint","IMPRINT",FACE,{"disambiguationData":[TD([[makeQuery(id+"F20.imprint","IMPRINT",EDGE,{"derivedFrom":sQuery(id+"F20.wireOp",EDGE,"E85.8.0.0")}),-1.0]])]});
            extrude(context, id + "F22", {"entities" : qUnion([Q0, Q1, Q2, Q3, Q4, Q5, Q6, Q7, Q8]), "operationType" : NewBodyOperationType.ADD, "depth" : 41.9 * mm});
        }
        {
            var Q0;
            Q0=makeQuery(id+"F21.opExtrude","SWEPT_FACE",FACE,{"disambiguationData":[OSD([sQuery(id+"F20.wireOp",EDGE,"E83.top")])]});
            var sketch = newSketch(context, id + "F23", { "sketchPlane" : qUnion([Q0])});
            skLineSegment(sketch, "E87.0", {"start": v(-469.9, -73.03) * mm, "end": v(469.9, -73.03) * mm});
            skLineSegment(sketch, "E87.1", {"start": v(469.9, -73.03) * mm, "end": v(469.9, -111.13) * mm});
            skLineSegment(sketch, "E87.2", {"start": v(-469.9, -111.13) * mm, "end": v(469.9, -111.13) * mm});
            skCircle(sketch, "E88", {"center": v(436.88, -92.08) * mm, "radius": 5.08 * mm});
            skPoint(sketch, "E88.centerSnap0", {"position": v(469.9, -92.08) * mm});
            skSolve(sketch);
        }
        {
            var Q0;
            Q0=sQuery(id+"F23.wireOp",EDGE,"E88");
            extrude(context, id + "F24", {"bodyType" : ToolBodyType.SURFACE, "surfaceEntities" : qUnion([Q0]), "depth" : 304.8 * mm});
        }
        {
            var Q0;
            Q0=makeQuery(id+"F13.opPattern","COPY",FACE,{"derivedFrom":makeQuery(id+"F1.opExtrude","CAP_FACE",FACE,{"disambiguationData":[OSD([sQuery(id+"F0.wireOp",EDGE,"E0.bottom"),sQuery(id+"F0.wireOp",EDGE,"E0.top"),sQuery(id+"F0.wireOp",EDGE,"E0.left"),sQuery(id+"F0.wireOp",EDGE,"E1.top"),sQuery(id+"F0.wireOp",EDGE,"E1.right"),sQuery(id+"F0.wireOp",EDGE,"E2.0.1.1"),sQuery(id+"F0.wireOp",EDGE,"E2.0.1.2"),sQuery(id+"F0.wireOp",EDGE,"E2.0.1.3"),sQuery(id+"F0.wireOp",EDGE,"E2.0.2.1"),sQuery(id+"F0.wireOp",EDGE,"E2.0.2.2"),sQuery(id+"F0.wireOp",EDGE,"E2.0.2.3"),sQuery(id+"F0.wireOp",EDGE,"E2.0.3.1"),sQuery(id+"F0.wireOp",EDGE,"E2.0.3.2"),sQuery(id+"F0.wireOp",EDGE,"E2.0.3.3"),sQuery(id+"F0.wireOp",EDGE,"E2.0.4.1"),sQuery(id+"F0.wireOp",EDGE,"E2.0.4.2"),sQuery(id+"F0.wireOp",EDGE,"E2.0.4.3"),sQuery(id+"F0.wireOp",EDGE,"E2.0.5.1"),sQuery(id+"F0.wireOp",EDGE,"E2.0.5.2"),sQuery(id+"F0.wireOp",EDGE,"E2.0.5.3"),sQuery(id+"F0.wireOp",EDGE,"E2.0.6.1"),sQuery(id+"F0.wireOp",EDGE,"E2.0.6.2"),sQuery(id+"F0.wireOp",EDGE,"E2.0.6.3"),sQuery(id+"F0.wireOp",EDGE,"E2.0.7.1"),sQuery(id+"F0.wireOp",EDGE,"E2.0.7.2"),sQuery(id+"F0.wireOp",EDGE,"E2.0.7.3"),sQuery(id+"F0.wireOp",EDGE,"E5.MirrorCS"),sQuery(id+"F0.wireOp",EDGE,"E7.MirrorCS"),sQuery(id+"F0.wireOp",EDGE,"E8.MirrorCS"),sQuery(id+"F0.wireOp",EDGE,"E10.MirrorCS"),sQuery(id+"F0.wireOp",EDGE,"E11.MirrorCS"),sQuery(id+"F0.wireOp",EDGE,"E12.MirrorCS"),sQuery(id+"F0.wireOp",EDGE,"E14.MirrorCS"),sQuery(id+"F0.wireOp",EDGE,"E15.MirrorCS"),sQuery(id+"F0.wireOp",EDGE,"E16.MirrorCS"),sQuery(id+"F0.wireOp",EDGE,"E18.MirrorCS"),sQuery(id+"F0.wireOp",EDGE,"E19.MirrorCS"),sQuery(id+"F0.wireOp",EDGE,"E21.MirrorCS"),sQuery(id+"F0.wireOp",EDGE,"E24.MirrorCS"),sQuery(id+"F0.wireOp",EDGE,"E25.MirrorCS"),sQuery(id+"F0.wireOp",EDGE,"E26.MirrorCS"),sQuery(id+"F0.wireOp",EDGE,"E27.MirrorCS"),sQuery(id+"F0.wireOp",EDGE,"E28.MirrorCS"),sQuery(id+"F0.wireOp",EDGE,"E29.MirrorCS"),sQuery(id+"F0.wireOp",EDGE,"E30.MirrorCS"),sQuery(id+"F0.wireOp",EDGE,"E31.MirrorCS"),sQuery(id+"F0.wireOp",EDGE,"E32.MirrorCS"),sQuery(id+"F0.wireOp",EDGE,"E33.MirrorCS"),sQuery(id+"F0.wireOp",EDGE,"E34.MirrorCS"),sQuery(id+"F0.wireOp",EDGE,"E35.MirrorCS"),sQuery(id+"F0.wireOp",EDGE,"E38.MirrorCS"),sQuery(id+"F0.wireOp",EDGE,"E39.MirrorCS")])],"isStart":true}),"instanceName":"1"});
            var sketch = newSketch(context, id + "F25", { "sketchPlane" : qUnion([Q0])});
            skLineSegment(sketch, "E89.0", {"start": v(325.12, -69.22) * mm, "end": v(353.06, -69.22) * mm, "construction": true});
            skPoint(sketch, "E90", {"position": v(339.09, -69.22) * mm});
            skLineSegment(sketch, "E91.rect.bottom", {"start": v(339.09, -44.45) * mm, "end": v(339.09, -44.45) * mm});
            skLineSegment(sketch, "E91.rect.top", {"start": v(339.09, 44.45) * mm, "end": v(339.09, 44.45) * mm});
            skLineSegment(sketch, "E91.rect.left", {"start": v(358.14, -25.4) * mm, "end": v(358.14, 25.4) * mm});
            skLineSegment(sketch, "E91.rect.right", {"start": v(320.04, -25.4) * mm, "end": v(320.04, 25.4) * mm});
            skPoint(sketch, "E91.rect.middle", {"position": v(339.09, 0) * mm});
            skPoint(sketch, "E92.visualSharp", {"position": v(320.04, 44.45) * mm});
            skArc(sketch, "E92.filletArc", {"start": v(339.09, 44.45) * mm, "mid": v(325.62, 38.87) * mm, "end": v(320.04, 25.4) * mm});
            skPoint(sketch, "E93.visualSharp", {"position": v(358.14, 44.45) * mm});
            skArc(sketch, "E93.filletArc", {"start": v(358.14, 25.4) * mm, "mid": v(352.56, 38.87) * mm, "end": v(339.09, 44.45) * mm});
            skPoint(sketch, "E94.visualSharp", {"position": v(358.14, -44.45) * mm});
            skArc(sketch, "E94.filletArc", {"start": v(339.09, -44.45) * mm, "mid": v(352.56, -38.87) * mm, "end": v(358.14, -25.4) * mm});
            skPoint(sketch, "E95.visualSharp", {"position": v(320.04, -44.45) * mm});
            skArc(sketch, "E95.filletArc", {"start": v(320.04, -25.4) * mm, "mid": v(325.62, -38.87) * mm, "end": v(339.09, -44.45) * mm});
            skArc(sketch, "E96.1.0.0", {"start": v(224.79, -25.4) * mm, "mid": v(230.37, -38.87) * mm, "end": v(243.84, -44.45) * mm});
            skLineSegment(sketch, "E96.1.0.1", {"start": v(224.79, -25.4) * mm, "end": v(224.79, 25.4) * mm});
            skArc(sketch, "E96.1.0.2", {"start": v(243.84, 44.45) * mm, "mid": v(230.37, 38.87) * mm, "end": v(224.79, 25.4) * mm});
            skArc(sketch, "E96.1.0.3", {"start": v(262.89, 25.4) * mm, "mid": v(257.31, 38.87) * mm, "end": v(243.84, 44.45) * mm});
            skLineSegment(sketch, "E96.1.0.4", {"start": v(262.89, -25.4) * mm, "end": v(262.89, 25.4) * mm});
            skArc(sketch, "E96.1.0.5", {"start": v(243.84, -44.45) * mm, "mid": v(257.31, -38.87) * mm, "end": v(262.89, -25.4) * mm});
            skArc(sketch, "E96.2.0.0", {"start": v(129.54, -25.4) * mm, "mid": v(135.12, -38.87) * mm, "end": v(148.59, -44.45) * mm});
            skLineSegment(sketch, "E96.2.0.1", {"start": v(129.54, -25.4) * mm, "end": v(129.54, 25.4) * mm});
            skArc(sketch, "E96.2.0.2", {"start": v(148.59, 44.45) * mm, "mid": v(135.12, 38.87) * mm, "end": v(129.54, 25.4) * mm});
            skArc(sketch, "E96.2.0.3", {"start": v(167.64, 25.4) * mm, "mid": v(162.06, 38.87) * mm, "end": v(148.59, 44.45) * mm});
            skLineSegment(sketch, "E96.2.0.4", {"start": v(167.64, -25.4) * mm, "end": v(167.64, 25.4) * mm});
            skArc(sketch, "E96.2.0.5", {"start": v(148.59, -44.45) * mm, "mid": v(162.06, -38.87) * mm, "end": v(167.64, -25.4) * mm});
            skArc(sketch, "E96.3.0.0", {"start": v(34.29, -25.4) * mm, "mid": v(39.87, -38.87) * mm, "end": v(53.34, -44.45) * mm});
            skLineSegment(sketch, "E96.3.0.1", {"start": v(34.29, -25.4) * mm, "end": v(34.29, 25.4) * mm});
            skArc(sketch, "E96.3.0.2", {"start": v(53.34, 44.45) * mm, "mid": v(39.87, 38.87) * mm, "end": v(34.29, 25.4) * mm});
            skArc(sketch, "E96.3.0.3", {"start": v(72.39, 25.4) * mm, "mid": v(66.81, 38.87) * mm, "end": v(53.34, 44.45) * mm});
            skLineSegment(sketch, "E96.3.0.4", {"start": v(72.39, -25.4) * mm, "end": v(72.39, 25.4) * mm});
            skArc(sketch, "E96.3.0.5", {"start": v(53.34, -44.45) * mm, "mid": v(66.81, -38.87) * mm, "end": v(72.39, -25.4) * mm});
            skArc(sketch, "E96.4.0.0", {"start": v(-60.96, -25.4) * mm, "mid": v(-55.38, -38.87) * mm, "end": v(-41.91, -44.45) * mm});
            skLineSegment(sketch, "E96.4.0.1", {"start": v(-60.96, -25.4) * mm, "end": v(-60.96, 25.4) * mm});
            skArc(sketch, "E96.4.0.2", {"start": v(-41.91, 44.45) * mm, "mid": v(-55.38, 38.87) * mm, "end": v(-60.96, 25.4) * mm});
            skArc(sketch, "E96.4.0.3", {"start": v(-22.86, 25.4) * mm, "mid": v(-28.44, 38.87) * mm, "end": v(-41.91, 44.45) * mm});
            skLineSegment(sketch, "E96.4.0.4", {"start": v(-22.86, -25.4) * mm, "end": v(-22.86, 25.4) * mm});
            skArc(sketch, "E96.4.0.5", {"start": v(-41.91, -44.45) * mm, "mid": v(-28.44, -38.87) * mm, "end": v(-22.86, -25.4) * mm});
            skArc(sketch, "E96.5.0.0", {"start": v(-156.21, -25.4) * mm, "mid": v(-150.63, -38.87) * mm, "end": v(-137.16, -44.45) * mm});
            skLineSegment(sketch, "E96.5.0.1", {"start": v(-156.21, -25.4) * mm, "end": v(-156.21, 25.4) * mm});
            skArc(sketch, "E96.5.0.2", {"start": v(-137.16, 44.45) * mm, "mid": v(-150.63, 38.87) * mm, "end": v(-156.21, 25.4) * mm});
            skArc(sketch, "E96.5.0.3", {"start": v(-118.11, 25.4) * mm, "mid": v(-123.69, 38.87) * mm, "end": v(-137.16, 44.45) * mm});
            skLineSegment(sketch, "E96.5.0.4", {"start": v(-118.11, -25.4) * mm, "end": v(-118.11, 25.4) * mm});
            skArc(sketch, "E96.5.0.5", {"start": v(-137.16, -44.45) * mm, "mid": v(-123.69, -38.87) * mm, "end": v(-118.11, -25.4) * mm});
            skArc(sketch, "E96.6.0.0", {"start": v(-251.46, -25.4) * mm, "mid": v(-245.88, -38.87) * mm, "end": v(-232.41, -44.45) * mm});
            skLineSegment(sketch, "E96.6.0.1", {"start": v(-251.46, -25.4) * mm, "end": v(-251.46, 25.4) * mm});
            skArc(sketch, "E96.6.0.2", {"start": v(-232.41, 44.45) * mm, "mid": v(-245.88, 38.87) * mm, "end": v(-251.46, 25.4) * mm});
            skArc(sketch, "E96.6.0.3", {"start": v(-213.36, 25.4) * mm, "mid": v(-218.94, 38.87) * mm, "end": v(-232.41, 44.45) * mm});
            skLineSegment(sketch, "E96.6.0.4", {"start": v(-213.36, -25.4) * mm, "end": v(-213.36, 25.4) * mm});
            skArc(sketch, "E96.6.0.5", {"start": v(-232.41, -44.45) * mm, "mid": v(-218.94, -38.87) * mm, "end": v(-213.36, -25.4) * mm});
            skArc(sketch, "E96.7.0.0", {"start": v(-346.71, -25.4) * mm, "mid": v(-341.13, -38.87) * mm, "end": v(-327.66, -44.45) * mm});
            skLineSegment(sketch, "E96.7.0.1", {"start": v(-346.71, -25.4) * mm, "end": v(-346.71, 25.4) * mm});
            skArc(sketch, "E96.7.0.2", {"start": v(-327.66, 44.45) * mm, "mid": v(-341.13, 38.87) * mm, "end": v(-346.71, 25.4) * mm});
            skArc(sketch, "E96.7.0.3", {"start": v(-308.61, 25.4) * mm, "mid": v(-314.19, 38.87) * mm, "end": v(-327.66, 44.45) * mm});
            skLineSegment(sketch, "E96.7.0.4", {"start": v(-308.61, -25.4) * mm, "end": v(-308.61, 25.4) * mm});
            skArc(sketch, "E96.7.0.5", {"start": v(-327.66, -44.45) * mm, "mid": v(-314.19, -38.87) * mm, "end": v(-308.61, -25.4) * mm});
            skArc(sketch, "E96.8.0.0", {"start": v(-441.96, -25.4) * mm, "mid": v(-436.38, -38.87) * mm, "end": v(-422.91, -44.45) * mm});
            skLineSegment(sketch, "E96.8.0.1", {"start": v(-441.96, -25.4) * mm, "end": v(-441.96, 25.4) * mm});
            skArc(sketch, "E96.8.0.2", {"start": v(-422.91, 44.45) * mm, "mid": v(-436.38, 38.87) * mm, "end": v(-441.96, 25.4) * mm});
            skArc(sketch, "E96.8.0.3", {"start": v(-403.86, 25.4) * mm, "mid": v(-409.44, 38.87) * mm, "end": v(-422.91, 44.45) * mm});
            skLineSegment(sketch, "E96.8.0.4", {"start": v(-403.86, -25.4) * mm, "end": v(-403.86, 25.4) * mm});
            skArc(sketch, "E96.8.0.5", {"start": v(-422.91, -44.45) * mm, "mid": v(-409.44, -38.87) * mm, "end": v(-403.86, -25.4) * mm});
            skLineSegment(sketch, "E96.direction1", {"start": v(339.09, -44.45) * mm, "end": v(243.84, -44.45) * mm, "construction": true});
            skSolve(sketch);
        }
        {
            var Q0;
            Q0 = qSketchRegion(id + "F25", true);
            var Q1;
            Q1=makeQuery(id+"F25.imprint","IMPRINT",FACE,{"disambiguationData":[TD([[makeQuery(id+"F25.imprint","IMPRINT",EDGE,{"derivedFrom":sQuery(id+"F25.wireOp",EDGE,"E96.8.0.0")}),1.0]])]});
            extrude(context, id + "F26", {"entities" : qUnion([Q0, Q1]), "operationType" : NewBodyOperationType.REMOVE, "endBound" : BoundingType.THROUGH_ALL, "oppositeDirection" : true, "depth" : 25.4 * mm});
        }
        {
            var Q0;
            Q0=makeQuery(id+"F26.boolean.opBoolean","INTERSECT",EDGE,{"derivedFrom":[makeQuery(id+"F13.opPattern","COPY",FACE,{"derivedFrom":makeQuery(id+"F1.opExtrude","CAP_FACE",FACE,{"disambiguationData":[OSD([sQuery(id+"F0.wireOp",EDGE,"E0.bottom"),sQuery(id+"F0.wireOp",EDGE,"E0.top"),sQuery(id+"F0.wireOp",EDGE,"E0.left"),sQuery(id+"F0.wireOp",EDGE,"E1.top"),sQuery(id+"F0.wireOp",EDGE,"E1.right"),sQuery(id+"F0.wireOp",EDGE,"E2.0.1.1"),sQuery(id+"F0.wireOp",EDGE,"E2.0.1.2"),sQuery(id+"F0.wireOp",EDGE,"E2.0.1.3"),sQuery(id+"F0.wireOp",EDGE,"E2.0.2.1"),sQuery(id+"F0.wireOp",EDGE,"E2.0.2.2"),sQuery(id+"F0.wireOp",EDGE,"E2.0.2.3"),sQuery(id+"F0.wireOp",EDGE,"E2.0.3.1"),sQuery(id+"F0.wireOp",EDGE,"E2.0.3.2"),sQuery(id+"F0.wireOp",EDGE,"E2.0.3.3"),sQuery(id+"F0.wireOp",EDGE,"E2.0.4.1"),sQuery(id+"F0.wireOp",EDGE,"E2.0.4.2"),sQuery(id+"F0.wireOp",EDGE,"E2.0.4.3"),sQuery(id+"F0.wireOp",EDGE,"E2.0.5.1"),sQuery(id+"F0.wireOp",EDGE,"E2.0.5.2"),sQuery(id+"F0.wireOp",EDGE,"E2.0.5.3"),sQuery(id+"F0.wireOp",EDGE,"E2.0.6.1"),sQuery(id+"F0.wireOp",EDGE,"E2.0.6.2"),sQuery(id+"F0.wireOp",EDGE,"E2.0.6.3"),sQuery(id+"F0.wireOp",EDGE,"E2.0.7.1"),sQuery(id+"F0.wireOp",EDGE,"E2.0.7.2"),sQuery(id+"F0.wireOp",EDGE,"E2.0.7.3"),sQuery(id+"F0.wireOp",EDGE,"E5.MirrorCS"),sQuery(id+"F0.wireOp",EDGE,"E7.MirrorCS"),sQuery(id+"F0.wireOp",EDGE,"E8.MirrorCS"),sQuery(id+"F0.wireOp",EDGE,"E10.MirrorCS"),sQuery(id+"F0.wireOp",EDGE,"E11.MirrorCS"),sQuery(id+"F0.wireOp",EDGE,"E12.MirrorCS"),sQuery(id+"F0.wireOp",EDGE,"E14.MirrorCS"),sQuery(id+"F0.wireOp",EDGE,"E15.MirrorCS"),sQuery(id+"F0.wireOp",EDGE,"E16.MirrorCS"),sQuery(id+"F0.wireOp",EDGE,"E18.MirrorCS"),sQuery(id+"F0.wireOp",EDGE,"E19.MirrorCS"),sQuery(id+"F0.wireOp",EDGE,"E21.MirrorCS"),sQuery(id+"F0.wireOp",EDGE,"E24.MirrorCS"),sQuery(id+"F0.wireOp",EDGE,"E25.MirrorCS"),sQuery(id+"F0.wireOp",EDGE,"E26.MirrorCS"),sQuery(id+"F0.wireOp",EDGE,"E27.MirrorCS"),sQuery(id+"F0.wireOp",EDGE,"E28.MirrorCS"),sQuery(id+"F0.wireOp",EDGE,"E29.MirrorCS"),sQuery(id+"F0.wireOp",EDGE,"E30.MirrorCS"),sQuery(id+"F0.wireOp",EDGE,"E31.MirrorCS"),sQuery(id+"F0.wireOp",EDGE,"E32.MirrorCS"),sQuery(id+"F0.wireOp",EDGE,"E33.MirrorCS"),sQuery(id+"F0.wireOp",EDGE,"E34.MirrorCS"),sQuery(id+"F0.wireOp",EDGE,"E35.MirrorCS"),sQuery(id+"F0.wireOp",EDGE,"E38.MirrorCS"),sQuery(id+"F0.wireOp",EDGE,"E39.MirrorCS")])],"isStart":false}),"instanceName":"1"}),makeQuery(id+"F26.opExtrude","SWEPT_FACE",FACE,{"disambiguationData":[OSD([sQuery(id+"F25.wireOp",EDGE,"E96.8.0.1")])]})]});
            var Q1;
            Q1=makeQuery(id+"F26.boolean.opBoolean","INTERSECT",EDGE,{"derivedFrom":[makeQuery(id+"F13.opPattern","COPY",FACE,{"derivedFrom":makeQuery(id+"F1.opExtrude","CAP_FACE",FACE,{"disambiguationData":[OSD([sQuery(id+"F0.wireOp",EDGE,"E0.bottom"),sQuery(id+"F0.wireOp",EDGE,"E0.top"),sQuery(id+"F0.wireOp",EDGE,"E0.left"),sQuery(id+"F0.wireOp",EDGE,"E1.top"),sQuery(id+"F0.wireOp",EDGE,"E1.right"),sQuery(id+"F0.wireOp",EDGE,"E2.0.1.1"),sQuery(id+"F0.wireOp",EDGE,"E2.0.1.2"),sQuery(id+"F0.wireOp",EDGE,"E2.0.1.3"),sQuery(id+"F0.wireOp",EDGE,"E2.0.2.1"),sQuery(id+"F0.wireOp",EDGE,"E2.0.2.2"),sQuery(id+"F0.wireOp",EDGE,"E2.0.2.3"),sQuery(id+"F0.wireOp",EDGE,"E2.0.3.1"),sQuery(id+"F0.wireOp",EDGE,"E2.0.3.2"),sQuery(id+"F0.wireOp",EDGE,"E2.0.3.3"),sQuery(id+"F0.wireOp",EDGE,"E2.0.4.1"),sQuery(id+"F0.wireOp",EDGE,"E2.0.4.2"),sQuery(id+"F0.wireOp",EDGE,"E2.0.4.3"),sQuery(id+"F0.wireOp",EDGE,"E2.0.5.1"),sQuery(id+"F0.wireOp",EDGE,"E2.0.5.2"),sQuery(id+"F0.wireOp",EDGE,"E2.0.5.3"),sQuery(id+"F0.wireOp",EDGE,"E2.0.6.1"),sQuery(id+"F0.wireOp",EDGE,"E2.0.6.2"),sQuery(id+"F0.wireOp",EDGE,"E2.0.6.3"),sQuery(id+"F0.wireOp",EDGE,"E2.0.7.1"),sQuery(id+"F0.wireOp",EDGE,"E2.0.7.2"),sQuery(id+"F0.wireOp",EDGE,"E2.0.7.3"),sQuery(id+"F0.wireOp",EDGE,"E5.MirrorCS"),sQuery(id+"F0.wireOp",EDGE,"E7.MirrorCS"),sQuery(id+"F0.wireOp",EDGE,"E8.MirrorCS"),sQuery(id+"F0.wireOp",EDGE,"E10.MirrorCS"),sQuery(id+"F0.wireOp",EDGE,"E11.MirrorCS"),sQuery(id+"F0.wireOp",EDGE,"E12.MirrorCS"),sQuery(id+"F0.wireOp",EDGE,"E14.MirrorCS"),sQuery(id+"F0.wireOp",EDGE,"E15.MirrorCS"),sQuery(id+"F0.wireOp",EDGE,"E16.MirrorCS"),sQuery(id+"F0.wireOp",EDGE,"E18.MirrorCS"),sQuery(id+"F0.wireOp",EDGE,"E19.MirrorCS"),sQuery(id+"F0.wireOp",EDGE,"E21.MirrorCS"),sQuery(id+"F0.wireOp",EDGE,"E24.MirrorCS"),sQuery(id+"F0.wireOp",EDGE,"E25.MirrorCS"),sQuery(id+"F0.wireOp",EDGE,"E26.MirrorCS"),sQuery(id+"F0.wireOp",EDGE,"E27.MirrorCS"),sQuery(id+"F0.wireOp",EDGE,"E28.MirrorCS"),sQuery(id+"F0.wireOp",EDGE,"E29.MirrorCS"),sQuery(id+"F0.wireOp",EDGE,"E30.MirrorCS"),sQuery(id+"F0.wireOp",EDGE,"E31.MirrorCS"),sQuery(id+"F0.wireOp",EDGE,"E32.MirrorCS"),sQuery(id+"F0.wireOp",EDGE,"E33.MirrorCS"),sQuery(id+"F0.wireOp",EDGE,"E34.MirrorCS"),sQuery(id+"F0.wireOp",EDGE,"E35.MirrorCS"),sQuery(id+"F0.wireOp",EDGE,"E38.MirrorCS"),sQuery(id+"F0.wireOp",EDGE,"E39.MirrorCS")])],"isStart":false}),"instanceName":"1"}),makeQuery(id+"F26.opExtrude","SWEPT_FACE",FACE,{"disambiguationData":[OSD([sQuery(id+"F25.wireOp",EDGE,"E96.7.0.1")])]})]});
            var Q2;
            Q2=makeQuery(id+"F26.boolean.opBoolean","INTERSECT",EDGE,{"derivedFrom":[makeQuery(id+"F13.opPattern","COPY",FACE,{"derivedFrom":makeQuery(id+"F1.opExtrude","CAP_FACE",FACE,{"disambiguationData":[OSD([sQuery(id+"F0.wireOp",EDGE,"E0.bottom"),sQuery(id+"F0.wireOp",EDGE,"E0.top"),sQuery(id+"F0.wireOp",EDGE,"E0.left"),sQuery(id+"F0.wireOp",EDGE,"E1.top"),sQuery(id+"F0.wireOp",EDGE,"E1.right"),sQuery(id+"F0.wireOp",EDGE,"E2.0.1.1"),sQuery(id+"F0.wireOp",EDGE,"E2.0.1.2"),sQuery(id+"F0.wireOp",EDGE,"E2.0.1.3"),sQuery(id+"F0.wireOp",EDGE,"E2.0.2.1"),sQuery(id+"F0.wireOp",EDGE,"E2.0.2.2"),sQuery(id+"F0.wireOp",EDGE,"E2.0.2.3"),sQuery(id+"F0.wireOp",EDGE,"E2.0.3.1"),sQuery(id+"F0.wireOp",EDGE,"E2.0.3.2"),sQuery(id+"F0.wireOp",EDGE,"E2.0.3.3"),sQuery(id+"F0.wireOp",EDGE,"E2.0.4.1"),sQuery(id+"F0.wireOp",EDGE,"E2.0.4.2"),sQuery(id+"F0.wireOp",EDGE,"E2.0.4.3"),sQuery(id+"F0.wireOp",EDGE,"E2.0.5.1"),sQuery(id+"F0.wireOp",EDGE,"E2.0.5.2"),sQuery(id+"F0.wireOp",EDGE,"E2.0.5.3"),sQuery(id+"F0.wireOp",EDGE,"E2.0.6.1"),sQuery(id+"F0.wireOp",EDGE,"E2.0.6.2"),sQuery(id+"F0.wireOp",EDGE,"E2.0.6.3"),sQuery(id+"F0.wireOp",EDGE,"E2.0.7.1"),sQuery(id+"F0.wireOp",EDGE,"E2.0.7.2"),sQuery(id+"F0.wireOp",EDGE,"E2.0.7.3"),sQuery(id+"F0.wireOp",EDGE,"E5.MirrorCS"),sQuery(id+"F0.wireOp",EDGE,"E7.MirrorCS"),sQuery(id+"F0.wireOp",EDGE,"E8.MirrorCS"),sQuery(id+"F0.wireOp",EDGE,"E10.MirrorCS"),sQuery(id+"F0.wireOp",EDGE,"E11.MirrorCS"),sQuery(id+"F0.wireOp",EDGE,"E12.MirrorCS"),sQuery(id+"F0.wireOp",EDGE,"E14.MirrorCS"),sQuery(id+"F0.wireOp",EDGE,"E15.MirrorCS"),sQuery(id+"F0.wireOp",EDGE,"E16.MirrorCS"),sQuery(id+"F0.wireOp",EDGE,"E18.MirrorCS"),sQuery(id+"F0.wireOp",EDGE,"E19.MirrorCS"),sQuery(id+"F0.wireOp",EDGE,"E21.MirrorCS"),sQuery(id+"F0.wireOp",EDGE,"E24.MirrorCS"),sQuery(id+"F0.wireOp",EDGE,"E25.MirrorCS"),sQuery(id+"F0.wireOp",EDGE,"E26.MirrorCS"),sQuery(id+"F0.wireOp",EDGE,"E27.MirrorCS"),sQuery(id+"F0.wireOp",EDGE,"E28.MirrorCS"),sQuery(id+"F0.wireOp",EDGE,"E29.MirrorCS"),sQuery(id+"F0.wireOp",EDGE,"E30.MirrorCS"),sQuery(id+"F0.wireOp",EDGE,"E31.MirrorCS"),sQuery(id+"F0.wireOp",EDGE,"E32.MirrorCS"),sQuery(id+"F0.wireOp",EDGE,"E33.MirrorCS"),sQuery(id+"F0.wireOp",EDGE,"E34.MirrorCS"),sQuery(id+"F0.wireOp",EDGE,"E35.MirrorCS"),sQuery(id+"F0.wireOp",EDGE,"E38.MirrorCS"),sQuery(id+"F0.wireOp",EDGE,"E39.MirrorCS")])],"isStart":false}),"instanceName":"1"}),makeQuery(id+"F26.opExtrude","SWEPT_FACE",FACE,{"disambiguationData":[OSD([sQuery(id+"F25.wireOp",EDGE,"E96.6.0.1")])]})]});
            var Q3;
            Q3=makeQuery(id+"F26.boolean.opBoolean","INTERSECT",EDGE,{"derivedFrom":[makeQuery(id+"F13.opPattern","COPY",FACE,{"derivedFrom":makeQuery(id+"F1.opExtrude","CAP_FACE",FACE,{"disambiguationData":[OSD([sQuery(id+"F0.wireOp",EDGE,"E0.bottom"),sQuery(id+"F0.wireOp",EDGE,"E0.top"),sQuery(id+"F0.wireOp",EDGE,"E0.left"),sQuery(id+"F0.wireOp",EDGE,"E1.top"),sQuery(id+"F0.wireOp",EDGE,"E1.right"),sQuery(id+"F0.wireOp",EDGE,"E2.0.1.1"),sQuery(id+"F0.wireOp",EDGE,"E2.0.1.2"),sQuery(id+"F0.wireOp",EDGE,"E2.0.1.3"),sQuery(id+"F0.wireOp",EDGE,"E2.0.2.1"),sQuery(id+"F0.wireOp",EDGE,"E2.0.2.2"),sQuery(id+"F0.wireOp",EDGE,"E2.0.2.3"),sQuery(id+"F0.wireOp",EDGE,"E2.0.3.1"),sQuery(id+"F0.wireOp",EDGE,"E2.0.3.2"),sQuery(id+"F0.wireOp",EDGE,"E2.0.3.3"),sQuery(id+"F0.wireOp",EDGE,"E2.0.4.1"),sQuery(id+"F0.wireOp",EDGE,"E2.0.4.2"),sQuery(id+"F0.wireOp",EDGE,"E2.0.4.3"),sQuery(id+"F0.wireOp",EDGE,"E2.0.5.1"),sQuery(id+"F0.wireOp",EDGE,"E2.0.5.2"),sQuery(id+"F0.wireOp",EDGE,"E2.0.5.3"),sQuery(id+"F0.wireOp",EDGE,"E2.0.6.1"),sQuery(id+"F0.wireOp",EDGE,"E2.0.6.2"),sQuery(id+"F0.wireOp",EDGE,"E2.0.6.3"),sQuery(id+"F0.wireOp",EDGE,"E2.0.7.1"),sQuery(id+"F0.wireOp",EDGE,"E2.0.7.2"),sQuery(id+"F0.wireOp",EDGE,"E2.0.7.3"),sQuery(id+"F0.wireOp",EDGE,"E5.MirrorCS"),sQuery(id+"F0.wireOp",EDGE,"E7.MirrorCS"),sQuery(id+"F0.wireOp",EDGE,"E8.MirrorCS"),sQuery(id+"F0.wireOp",EDGE,"E10.MirrorCS"),sQuery(id+"F0.wireOp",EDGE,"E11.MirrorCS"),sQuery(id+"F0.wireOp",EDGE,"E12.MirrorCS"),sQuery(id+"F0.wireOp",EDGE,"E14.MirrorCS"),sQuery(id+"F0.wireOp",EDGE,"E15.MirrorCS"),sQuery(id+"F0.wireOp",EDGE,"E16.MirrorCS"),sQuery(id+"F0.wireOp",EDGE,"E18.MirrorCS"),sQuery(id+"F0.wireOp",EDGE,"E19.MirrorCS"),sQuery(id+"F0.wireOp",EDGE,"E21.MirrorCS"),sQuery(id+"F0.wireOp",EDGE,"E24.MirrorCS"),sQuery(id+"F0.wireOp",EDGE,"E25.MirrorCS"),sQuery(id+"F0.wireOp",EDGE,"E26.MirrorCS"),sQuery(id+"F0.wireOp",EDGE,"E27.MirrorCS"),sQuery(id+"F0.wireOp",EDGE,"E28.MirrorCS"),sQuery(id+"F0.wireOp",EDGE,"E29.MirrorCS"),sQuery(id+"F0.wireOp",EDGE,"E30.MirrorCS"),sQuery(id+"F0.wireOp",EDGE,"E31.MirrorCS"),sQuery(id+"F0.wireOp",EDGE,"E32.MirrorCS"),sQuery(id+"F0.wireOp",EDGE,"E33.MirrorCS"),sQuery(id+"F0.wireOp",EDGE,"E34.MirrorCS"),sQuery(id+"F0.wireOp",EDGE,"E35.MirrorCS"),sQuery(id+"F0.wireOp",EDGE,"E38.MirrorCS"),sQuery(id+"F0.wireOp",EDGE,"E39.MirrorCS")])],"isStart":false}),"instanceName":"1"}),makeQuery(id+"F26.opExtrude","SWEPT_FACE",FACE,{"disambiguationData":[OSD([sQuery(id+"F25.wireOp",EDGE,"E96.5.0.1")])]})]});
            var Q4;
            Q4=makeQuery(id+"F26.boolean.opBoolean","INTERSECT",EDGE,{"derivedFrom":[makeQuery(id+"F13.opPattern","COPY",FACE,{"derivedFrom":makeQuery(id+"F1.opExtrude","CAP_FACE",FACE,{"disambiguationData":[OSD([sQuery(id+"F0.wireOp",EDGE,"E0.bottom"),sQuery(id+"F0.wireOp",EDGE,"E0.top"),sQuery(id+"F0.wireOp",EDGE,"E0.left"),sQuery(id+"F0.wireOp",EDGE,"E1.top"),sQuery(id+"F0.wireOp",EDGE,"E1.right"),sQuery(id+"F0.wireOp",EDGE,"E2.0.1.1"),sQuery(id+"F0.wireOp",EDGE,"E2.0.1.2"),sQuery(id+"F0.wireOp",EDGE,"E2.0.1.3"),sQuery(id+"F0.wireOp",EDGE,"E2.0.2.1"),sQuery(id+"F0.wireOp",EDGE,"E2.0.2.2"),sQuery(id+"F0.wireOp",EDGE,"E2.0.2.3"),sQuery(id+"F0.wireOp",EDGE,"E2.0.3.1"),sQuery(id+"F0.wireOp",EDGE,"E2.0.3.2"),sQuery(id+"F0.wireOp",EDGE,"E2.0.3.3"),sQuery(id+"F0.wireOp",EDGE,"E2.0.4.1"),sQuery(id+"F0.wireOp",EDGE,"E2.0.4.2"),sQuery(id+"F0.wireOp",EDGE,"E2.0.4.3"),sQuery(id+"F0.wireOp",EDGE,"E2.0.5.1"),sQuery(id+"F0.wireOp",EDGE,"E2.0.5.2"),sQuery(id+"F0.wireOp",EDGE,"E2.0.5.3"),sQuery(id+"F0.wireOp",EDGE,"E2.0.6.1"),sQuery(id+"F0.wireOp",EDGE,"E2.0.6.2"),sQuery(id+"F0.wireOp",EDGE,"E2.0.6.3"),sQuery(id+"F0.wireOp",EDGE,"E2.0.7.1"),sQuery(id+"F0.wireOp",EDGE,"E2.0.7.2"),sQuery(id+"F0.wireOp",EDGE,"E2.0.7.3"),sQuery(id+"F0.wireOp",EDGE,"E5.MirrorCS"),sQuery(id+"F0.wireOp",EDGE,"E7.MirrorCS"),sQuery(id+"F0.wireOp",EDGE,"E8.MirrorCS"),sQuery(id+"F0.wireOp",EDGE,"E10.MirrorCS"),sQuery(id+"F0.wireOp",EDGE,"E11.MirrorCS"),sQuery(id+"F0.wireOp",EDGE,"E12.MirrorCS"),sQuery(id+"F0.wireOp",EDGE,"E14.MirrorCS"),sQuery(id+"F0.wireOp",EDGE,"E15.MirrorCS"),sQuery(id+"F0.wireOp",EDGE,"E16.MirrorCS"),sQuery(id+"F0.wireOp",EDGE,"E18.MirrorCS"),sQuery(id+"F0.wireOp",EDGE,"E19.MirrorCS"),sQuery(id+"F0.wireOp",EDGE,"E21.MirrorCS"),sQuery(id+"F0.wireOp",EDGE,"E24.MirrorCS"),sQuery(id+"F0.wireOp",EDGE,"E25.MirrorCS"),sQuery(id+"F0.wireOp",EDGE,"E26.MirrorCS"),sQuery(id+"F0.wireOp",EDGE,"E27.MirrorCS"),sQuery(id+"F0.wireOp",EDGE,"E28.MirrorCS"),sQuery(id+"F0.wireOp",EDGE,"E29.MirrorCS"),sQuery(id+"F0.wireOp",EDGE,"E30.MirrorCS"),sQuery(id+"F0.wireOp",EDGE,"E31.MirrorCS"),sQuery(id+"F0.wireOp",EDGE,"E32.MirrorCS"),sQuery(id+"F0.wireOp",EDGE,"E33.MirrorCS"),sQuery(id+"F0.wireOp",EDGE,"E34.MirrorCS"),sQuery(id+"F0.wireOp",EDGE,"E35.MirrorCS"),sQuery(id+"F0.wireOp",EDGE,"E38.MirrorCS"),sQuery(id+"F0.wireOp",EDGE,"E39.MirrorCS")])],"isStart":false}),"instanceName":"1"}),makeQuery(id+"F26.opExtrude","SWEPT_FACE",FACE,{"disambiguationData":[OSD([sQuery(id+"F25.wireOp",EDGE,"E96.4.0.1")])]})]});
            var Q5;
            Q5=makeQuery(id+"F26.boolean.opBoolean","INTERSECT",EDGE,{"derivedFrom":[makeQuery(id+"F13.opPattern","COPY",FACE,{"derivedFrom":makeQuery(id+"F1.opExtrude","CAP_FACE",FACE,{"disambiguationData":[OSD([sQuery(id+"F0.wireOp",EDGE,"E0.bottom"),sQuery(id+"F0.wireOp",EDGE,"E0.top"),sQuery(id+"F0.wireOp",EDGE,"E0.left"),sQuery(id+"F0.wireOp",EDGE,"E1.top"),sQuery(id+"F0.wireOp",EDGE,"E1.right"),sQuery(id+"F0.wireOp",EDGE,"E2.0.1.1"),sQuery(id+"F0.wireOp",EDGE,"E2.0.1.2"),sQuery(id+"F0.wireOp",EDGE,"E2.0.1.3"),sQuery(id+"F0.wireOp",EDGE,"E2.0.2.1"),sQuery(id+"F0.wireOp",EDGE,"E2.0.2.2"),sQuery(id+"F0.wireOp",EDGE,"E2.0.2.3"),sQuery(id+"F0.wireOp",EDGE,"E2.0.3.1"),sQuery(id+"F0.wireOp",EDGE,"E2.0.3.2"),sQuery(id+"F0.wireOp",EDGE,"E2.0.3.3"),sQuery(id+"F0.wireOp",EDGE,"E2.0.4.1"),sQuery(id+"F0.wireOp",EDGE,"E2.0.4.2"),sQuery(id+"F0.wireOp",EDGE,"E2.0.4.3"),sQuery(id+"F0.wireOp",EDGE,"E2.0.5.1"),sQuery(id+"F0.wireOp",EDGE,"E2.0.5.2"),sQuery(id+"F0.wireOp",EDGE,"E2.0.5.3"),sQuery(id+"F0.wireOp",EDGE,"E2.0.6.1"),sQuery(id+"F0.wireOp",EDGE,"E2.0.6.2"),sQuery(id+"F0.wireOp",EDGE,"E2.0.6.3"),sQuery(id+"F0.wireOp",EDGE,"E2.0.7.1"),sQuery(id+"F0.wireOp",EDGE,"E2.0.7.2"),sQuery(id+"F0.wireOp",EDGE,"E2.0.7.3"),sQuery(id+"F0.wireOp",EDGE,"E5.MirrorCS"),sQuery(id+"F0.wireOp",EDGE,"E7.MirrorCS"),sQuery(id+"F0.wireOp",EDGE,"E8.MirrorCS"),sQuery(id+"F0.wireOp",EDGE,"E10.MirrorCS"),sQuery(id+"F0.wireOp",EDGE,"E11.MirrorCS"),sQuery(id+"F0.wireOp",EDGE,"E12.MirrorCS"),sQuery(id+"F0.wireOp",EDGE,"E14.MirrorCS"),sQuery(id+"F0.wireOp",EDGE,"E15.MirrorCS"),sQuery(id+"F0.wireOp",EDGE,"E16.MirrorCS"),sQuery(id+"F0.wireOp",EDGE,"E18.MirrorCS"),sQuery(id+"F0.wireOp",EDGE,"E19.MirrorCS"),sQuery(id+"F0.wireOp",EDGE,"E21.MirrorCS"),sQuery(id+"F0.wireOp",EDGE,"E24.MirrorCS"),sQuery(id+"F0.wireOp",EDGE,"E25.MirrorCS"),sQuery(id+"F0.wireOp",EDGE,"E26.MirrorCS"),sQuery(id+"F0.wireOp",EDGE,"E27.MirrorCS"),sQuery(id+"F0.wireOp",EDGE,"E28.MirrorCS"),sQuery(id+"F0.wireOp",EDGE,"E29.MirrorCS"),sQuery(id+"F0.wireOp",EDGE,"E30.MirrorCS"),sQuery(id+"F0.wireOp",EDGE,"E31.MirrorCS"),sQuery(id+"F0.wireOp",EDGE,"E32.MirrorCS"),sQuery(id+"F0.wireOp",EDGE,"E33.MirrorCS"),sQuery(id+"F0.wireOp",EDGE,"E34.MirrorCS"),sQuery(id+"F0.wireOp",EDGE,"E35.MirrorCS"),sQuery(id+"F0.wireOp",EDGE,"E38.MirrorCS"),sQuery(id+"F0.wireOp",EDGE,"E39.MirrorCS")])],"isStart":false}),"instanceName":"1"}),makeQuery(id+"F26.opExtrude","SWEPT_FACE",FACE,{"disambiguationData":[OSD([sQuery(id+"F25.wireOp",EDGE,"E96.3.0.1")])]})]});
            var Q6;
            Q6=makeQuery(id+"F26.boolean.opBoolean","INTERSECT",EDGE,{"derivedFrom":[makeQuery(id+"F13.opPattern","COPY",FACE,{"derivedFrom":makeQuery(id+"F1.opExtrude","CAP_FACE",FACE,{"disambiguationData":[OSD([sQuery(id+"F0.wireOp",EDGE,"E0.bottom"),sQuery(id+"F0.wireOp",EDGE,"E0.top"),sQuery(id+"F0.wireOp",EDGE,"E0.left"),sQuery(id+"F0.wireOp",EDGE,"E1.top"),sQuery(id+"F0.wireOp",EDGE,"E1.right"),sQuery(id+"F0.wireOp",EDGE,"E2.0.1.1"),sQuery(id+"F0.wireOp",EDGE,"E2.0.1.2"),sQuery(id+"F0.wireOp",EDGE,"E2.0.1.3"),sQuery(id+"F0.wireOp",EDGE,"E2.0.2.1"),sQuery(id+"F0.wireOp",EDGE,"E2.0.2.2"),sQuery(id+"F0.wireOp",EDGE,"E2.0.2.3"),sQuery(id+"F0.wireOp",EDGE,"E2.0.3.1"),sQuery(id+"F0.wireOp",EDGE,"E2.0.3.2"),sQuery(id+"F0.wireOp",EDGE,"E2.0.3.3"),sQuery(id+"F0.wireOp",EDGE,"E2.0.4.1"),sQuery(id+"F0.wireOp",EDGE,"E2.0.4.2"),sQuery(id+"F0.wireOp",EDGE,"E2.0.4.3"),sQuery(id+"F0.wireOp",EDGE,"E2.0.5.1"),sQuery(id+"F0.wireOp",EDGE,"E2.0.5.2"),sQuery(id+"F0.wireOp",EDGE,"E2.0.5.3"),sQuery(id+"F0.wireOp",EDGE,"E2.0.6.1"),sQuery(id+"F0.wireOp",EDGE,"E2.0.6.2"),sQuery(id+"F0.wireOp",EDGE,"E2.0.6.3"),sQuery(id+"F0.wireOp",EDGE,"E2.0.7.1"),sQuery(id+"F0.wireOp",EDGE,"E2.0.7.2"),sQuery(id+"F0.wireOp",EDGE,"E2.0.7.3"),sQuery(id+"F0.wireOp",EDGE,"E5.MirrorCS"),sQuery(id+"F0.wireOp",EDGE,"E7.MirrorCS"),sQuery(id+"F0.wireOp",EDGE,"E8.MirrorCS"),sQuery(id+"F0.wireOp",EDGE,"E10.MirrorCS"),sQuery(id+"F0.wireOp",EDGE,"E11.MirrorCS"),sQuery(id+"F0.wireOp",EDGE,"E12.MirrorCS"),sQuery(id+"F0.wireOp",EDGE,"E14.MirrorCS"),sQuery(id+"F0.wireOp",EDGE,"E15.MirrorCS"),sQuery(id+"F0.wireOp",EDGE,"E16.MirrorCS"),sQuery(id+"F0.wireOp",EDGE,"E18.MirrorCS"),sQuery(id+"F0.wireOp",EDGE,"E19.MirrorCS"),sQuery(id+"F0.wireOp",EDGE,"E21.MirrorCS"),sQuery(id+"F0.wireOp",EDGE,"E24.MirrorCS"),sQuery(id+"F0.wireOp",EDGE,"E25.MirrorCS"),sQuery(id+"F0.wireOp",EDGE,"E26.MirrorCS"),sQuery(id+"F0.wireOp",EDGE,"E27.MirrorCS"),sQuery(id+"F0.wireOp",EDGE,"E28.MirrorCS"),sQuery(id+"F0.wireOp",EDGE,"E29.MirrorCS"),sQuery(id+"F0.wireOp",EDGE,"E30.MirrorCS"),sQuery(id+"F0.wireOp",EDGE,"E31.MirrorCS"),sQuery(id+"F0.wireOp",EDGE,"E32.MirrorCS"),sQuery(id+"F0.wireOp",EDGE,"E33.MirrorCS"),sQuery(id+"F0.wireOp",EDGE,"E34.MirrorCS"),sQuery(id+"F0.wireOp",EDGE,"E35.MirrorCS"),sQuery(id+"F0.wireOp",EDGE,"E38.MirrorCS"),sQuery(id+"F0.wireOp",EDGE,"E39.MirrorCS")])],"isStart":false}),"instanceName":"1"}),makeQuery(id+"F26.opExtrude","SWEPT_FACE",FACE,{"disambiguationData":[OSD([sQuery(id+"F25.wireOp",EDGE,"E96.2.0.1")])]})]});
            var Q7;
            Q7=makeQuery(id+"F26.boolean.opBoolean","INTERSECT",EDGE,{"derivedFrom":[makeQuery(id+"F13.opPattern","COPY",FACE,{"derivedFrom":makeQuery(id+"F1.opExtrude","CAP_FACE",FACE,{"disambiguationData":[OSD([sQuery(id+"F0.wireOp",EDGE,"E0.bottom"),sQuery(id+"F0.wireOp",EDGE,"E0.top"),sQuery(id+"F0.wireOp",EDGE,"E0.left"),sQuery(id+"F0.wireOp",EDGE,"E1.top"),sQuery(id+"F0.wireOp",EDGE,"E1.right"),sQuery(id+"F0.wireOp",EDGE,"E2.0.1.1"),sQuery(id+"F0.wireOp",EDGE,"E2.0.1.2"),sQuery(id+"F0.wireOp",EDGE,"E2.0.1.3"),sQuery(id+"F0.wireOp",EDGE,"E2.0.2.1"),sQuery(id+"F0.wireOp",EDGE,"E2.0.2.2"),sQuery(id+"F0.wireOp",EDGE,"E2.0.2.3"),sQuery(id+"F0.wireOp",EDGE,"E2.0.3.1"),sQuery(id+"F0.wireOp",EDGE,"E2.0.3.2"),sQuery(id+"F0.wireOp",EDGE,"E2.0.3.3"),sQuery(id+"F0.wireOp",EDGE,"E2.0.4.1"),sQuery(id+"F0.wireOp",EDGE,"E2.0.4.2"),sQuery(id+"F0.wireOp",EDGE,"E2.0.4.3"),sQuery(id+"F0.wireOp",EDGE,"E2.0.5.1"),sQuery(id+"F0.wireOp",EDGE,"E2.0.5.2"),sQuery(id+"F0.wireOp",EDGE,"E2.0.5.3"),sQuery(id+"F0.wireOp",EDGE,"E2.0.6.1"),sQuery(id+"F0.wireOp",EDGE,"E2.0.6.2"),sQuery(id+"F0.wireOp",EDGE,"E2.0.6.3"),sQuery(id+"F0.wireOp",EDGE,"E2.0.7.1"),sQuery(id+"F0.wireOp",EDGE,"E2.0.7.2"),sQuery(id+"F0.wireOp",EDGE,"E2.0.7.3"),sQuery(id+"F0.wireOp",EDGE,"E5.MirrorCS"),sQuery(id+"F0.wireOp",EDGE,"E7.MirrorCS"),sQuery(id+"F0.wireOp",EDGE,"E8.MirrorCS"),sQuery(id+"F0.wireOp",EDGE,"E10.MirrorCS"),sQuery(id+"F0.wireOp",EDGE,"E11.MirrorCS"),sQuery(id+"F0.wireOp",EDGE,"E12.MirrorCS"),sQuery(id+"F0.wireOp",EDGE,"E14.MirrorCS"),sQuery(id+"F0.wireOp",EDGE,"E15.MirrorCS"),sQuery(id+"F0.wireOp",EDGE,"E16.MirrorCS"),sQuery(id+"F0.wireOp",EDGE,"E18.MirrorCS"),sQuery(id+"F0.wireOp",EDGE,"E19.MirrorCS"),sQuery(id+"F0.wireOp",EDGE,"E21.MirrorCS"),sQuery(id+"F0.wireOp",EDGE,"E24.MirrorCS"),sQuery(id+"F0.wireOp",EDGE,"E25.MirrorCS"),sQuery(id+"F0.wireOp",EDGE,"E26.MirrorCS"),sQuery(id+"F0.wireOp",EDGE,"E27.MirrorCS"),sQuery(id+"F0.wireOp",EDGE,"E28.MirrorCS"),sQuery(id+"F0.wireOp",EDGE,"E29.MirrorCS"),sQuery(id+"F0.wireOp",EDGE,"E30.MirrorCS"),sQuery(id+"F0.wireOp",EDGE,"E31.MirrorCS"),sQuery(id+"F0.wireOp",EDGE,"E32.MirrorCS"),sQuery(id+"F0.wireOp",EDGE,"E33.MirrorCS"),sQuery(id+"F0.wireOp",EDGE,"E34.MirrorCS"),sQuery(id+"F0.wireOp",EDGE,"E35.MirrorCS"),sQuery(id+"F0.wireOp",EDGE,"E38.MirrorCS"),sQuery(id+"F0.wireOp",EDGE,"E39.MirrorCS")])],"isStart":false}),"instanceName":"1"}),makeQuery(id+"F26.opExtrude","SWEPT_FACE",FACE,{"disambiguationData":[OSD([sQuery(id+"F25.wireOp",EDGE,"E96.1.0.1")])]})]});
            var Q8;
            Q8=makeQuery(id+"F26.boolean.opBoolean","INTERSECT",EDGE,{"derivedFrom":[makeQuery(id+"F13.opPattern","COPY",FACE,{"derivedFrom":makeQuery(id+"F1.opExtrude","CAP_FACE",FACE,{"disambiguationData":[OSD([sQuery(id+"F0.wireOp",EDGE,"E0.bottom"),sQuery(id+"F0.wireOp",EDGE,"E0.top"),sQuery(id+"F0.wireOp",EDGE,"E0.left"),sQuery(id+"F0.wireOp",EDGE,"E1.top"),sQuery(id+"F0.wireOp",EDGE,"E1.right"),sQuery(id+"F0.wireOp",EDGE,"E2.0.1.1"),sQuery(id+"F0.wireOp",EDGE,"E2.0.1.2"),sQuery(id+"F0.wireOp",EDGE,"E2.0.1.3"),sQuery(id+"F0.wireOp",EDGE,"E2.0.2.1"),sQuery(id+"F0.wireOp",EDGE,"E2.0.2.2"),sQuery(id+"F0.wireOp",EDGE,"E2.0.2.3"),sQuery(id+"F0.wireOp",EDGE,"E2.0.3.1"),sQuery(id+"F0.wireOp",EDGE,"E2.0.3.2"),sQuery(id+"F0.wireOp",EDGE,"E2.0.3.3"),sQuery(id+"F0.wireOp",EDGE,"E2.0.4.1"),sQuery(id+"F0.wireOp",EDGE,"E2.0.4.2"),sQuery(id+"F0.wireOp",EDGE,"E2.0.4.3"),sQuery(id+"F0.wireOp",EDGE,"E2.0.5.1"),sQuery(id+"F0.wireOp",EDGE,"E2.0.5.2"),sQuery(id+"F0.wireOp",EDGE,"E2.0.5.3"),sQuery(id+"F0.wireOp",EDGE,"E2.0.6.1"),sQuery(id+"F0.wireOp",EDGE,"E2.0.6.2"),sQuery(id+"F0.wireOp",EDGE,"E2.0.6.3"),sQuery(id+"F0.wireOp",EDGE,"E2.0.7.1"),sQuery(id+"F0.wireOp",EDGE,"E2.0.7.2"),sQuery(id+"F0.wireOp",EDGE,"E2.0.7.3"),sQuery(id+"F0.wireOp",EDGE,"E5.MirrorCS"),sQuery(id+"F0.wireOp",EDGE,"E7.MirrorCS"),sQuery(id+"F0.wireOp",EDGE,"E8.MirrorCS"),sQuery(id+"F0.wireOp",EDGE,"E10.MirrorCS"),sQuery(id+"F0.wireOp",EDGE,"E11.MirrorCS"),sQuery(id+"F0.wireOp",EDGE,"E12.MirrorCS"),sQuery(id+"F0.wireOp",EDGE,"E14.MirrorCS"),sQuery(id+"F0.wireOp",EDGE,"E15.MirrorCS"),sQuery(id+"F0.wireOp",EDGE,"E16.MirrorCS"),sQuery(id+"F0.wireOp",EDGE,"E18.MirrorCS"),sQuery(id+"F0.wireOp",EDGE,"E19.MirrorCS"),sQuery(id+"F0.wireOp",EDGE,"E21.MirrorCS"),sQuery(id+"F0.wireOp",EDGE,"E24.MirrorCS"),sQuery(id+"F0.wireOp",EDGE,"E25.MirrorCS"),sQuery(id+"F0.wireOp",EDGE,"E26.MirrorCS"),sQuery(id+"F0.wireOp",EDGE,"E27.MirrorCS"),sQuery(id+"F0.wireOp",EDGE,"E28.MirrorCS"),sQuery(id+"F0.wireOp",EDGE,"E29.MirrorCS"),sQuery(id+"F0.wireOp",EDGE,"E30.MirrorCS"),sQuery(id+"F0.wireOp",EDGE,"E31.MirrorCS"),sQuery(id+"F0.wireOp",EDGE,"E32.MirrorCS"),sQuery(id+"F0.wireOp",EDGE,"E33.MirrorCS"),sQuery(id+"F0.wireOp",EDGE,"E34.MirrorCS"),sQuery(id+"F0.wireOp",EDGE,"E35.MirrorCS"),sQuery(id+"F0.wireOp",EDGE,"E38.MirrorCS"),sQuery(id+"F0.wireOp",EDGE,"E39.MirrorCS")])],"isStart":false}),"instanceName":"1"}),makeQuery(id+"F26.opExtrude","SWEPT_FACE",FACE,{"disambiguationData":[OSD([sQuery(id+"F25.wireOp",EDGE,"E91.rect.right")])]})]});
            var Q9;
            Q9=makeQuery(id+"F26.boolean.opBoolean","COPY",EDGE,{"derivedFrom":makeQuery(id+"F26.opExtrude","CAP_EDGE",EDGE,{"disambiguationData":[OSD([sQuery(id+"F25.wireOp",EDGE,"E96.8.0.4")])],"isStart":true})});
            var Q10;
            Q10=makeQuery(id+"F26.boolean.opBoolean","COPY",EDGE,{"derivedFrom":makeQuery(id+"F26.opExtrude","CAP_EDGE",EDGE,{"disambiguationData":[OSD([sQuery(id+"F25.wireOp",EDGE,"E96.7.0.4")])],"isStart":true})});
            var Q11;
            Q11=makeQuery(id+"F26.boolean.opBoolean","COPY",EDGE,{"derivedFrom":makeQuery(id+"F26.opExtrude","CAP_EDGE",EDGE,{"disambiguationData":[OSD([sQuery(id+"F25.wireOp",EDGE,"E96.6.0.4")])],"isStart":true})});
            var Q12;
            Q12=makeQuery(id+"F26.boolean.opBoolean","COPY",EDGE,{"derivedFrom":makeQuery(id+"F26.opExtrude","CAP_EDGE",EDGE,{"disambiguationData":[OSD([sQuery(id+"F25.wireOp",EDGE,"E96.5.0.4")])],"isStart":true})});
            var Q13;
            Q13=makeQuery(id+"F26.boolean.opBoolean","COPY",EDGE,{"derivedFrom":makeQuery(id+"F26.opExtrude","CAP_EDGE",EDGE,{"disambiguationData":[OSD([sQuery(id+"F25.wireOp",EDGE,"E96.4.0.4")])],"isStart":true})});
            var Q14;
            Q14=makeQuery(id+"F26.boolean.opBoolean","COPY",EDGE,{"derivedFrom":makeQuery(id+"F26.opExtrude","CAP_EDGE",EDGE,{"disambiguationData":[OSD([sQuery(id+"F25.wireOp",EDGE,"E96.3.0.4")])],"isStart":true})});
            var Q15;
            Q15=makeQuery(id+"F26.boolean.opBoolean","COPY",EDGE,{"derivedFrom":makeQuery(id+"F26.opExtrude","CAP_EDGE",EDGE,{"disambiguationData":[OSD([sQuery(id+"F25.wireOp",EDGE,"E96.2.0.4")])],"isStart":true})});
            var Q16;
            Q16=makeQuery(id+"F26.boolean.opBoolean","COPY",EDGE,{"derivedFrom":makeQuery(id+"F26.opExtrude","CAP_EDGE",EDGE,{"disambiguationData":[OSD([sQuery(id+"F25.wireOp",EDGE,"E96.1.0.4")])],"isStart":true})});
            var Q17;
            Q17=makeQuery(id+"F26.boolean.opBoolean","COPY",EDGE,{"derivedFrom":makeQuery(id+"F26.opExtrude","CAP_EDGE",EDGE,{"disambiguationData":[OSD([sQuery(id+"F25.wireOp",EDGE,"E91.rect.left")])],"isStart":true})});
            fillet(context, id + "F27", {"entities" : qUnion([Q0, Q1, Q2, Q3, Q4, Q5, Q6, Q7, Q8, Q9, Q10, Q11, Q12, Q13, Q14, Q15, Q16, Q17]), "radius" : 3.17 * mm, "tangentPropagation" : true, "allowEdgeOverflow" : false});
        }
        {
            var Q0;
            Q0=makeQuery(id+"F13.opPattern","COPY",FACE,{"derivedFrom":makeQuery(id+"F1.opExtrude","CAP_FACE",FACE,{"disambiguationData":[OSD([sQuery(id+"F0.wireOp",EDGE,"E0.bottom"),sQuery(id+"F0.wireOp",EDGE,"E0.top"),sQuery(id+"F0.wireOp",EDGE,"E0.left"),sQuery(id+"F0.wireOp",EDGE,"E1.top"),sQuery(id+"F0.wireOp",EDGE,"E1.right"),sQuery(id+"F0.wireOp",EDGE,"E2.0.1.1"),sQuery(id+"F0.wireOp",EDGE,"E2.0.1.2"),sQuery(id+"F0.wireOp",EDGE,"E2.0.1.3"),sQuery(id+"F0.wireOp",EDGE,"E2.0.2.1"),sQuery(id+"F0.wireOp",EDGE,"E2.0.2.2"),sQuery(id+"F0.wireOp",EDGE,"E2.0.2.3"),sQuery(id+"F0.wireOp",EDGE,"E2.0.3.1"),sQuery(id+"F0.wireOp",EDGE,"E2.0.3.2"),sQuery(id+"F0.wireOp",EDGE,"E2.0.3.3"),sQuery(id+"F0.wireOp",EDGE,"E2.0.4.1"),sQuery(id+"F0.wireOp",EDGE,"E2.0.4.2"),sQuery(id+"F0.wireOp",EDGE,"E2.0.4.3"),sQuery(id+"F0.wireOp",EDGE,"E2.0.5.1"),sQuery(id+"F0.wireOp",EDGE,"E2.0.5.2"),sQuery(id+"F0.wireOp",EDGE,"E2.0.5.3"),sQuery(id+"F0.wireOp",EDGE,"E2.0.6.1"),sQuery(id+"F0.wireOp",EDGE,"E2.0.6.2"),sQuery(id+"F0.wireOp",EDGE,"E2.0.6.3"),sQuery(id+"F0.wireOp",EDGE,"E2.0.7.1"),sQuery(id+"F0.wireOp",EDGE,"E2.0.7.2"),sQuery(id+"F0.wireOp",EDGE,"E2.0.7.3"),sQuery(id+"F0.wireOp",EDGE,"E5.MirrorCS"),sQuery(id+"F0.wireOp",EDGE,"E7.MirrorCS"),sQuery(id+"F0.wireOp",EDGE,"E8.MirrorCS"),sQuery(id+"F0.wireOp",EDGE,"E10.MirrorCS"),sQuery(id+"F0.wireOp",EDGE,"E11.MirrorCS"),sQuery(id+"F0.wireOp",EDGE,"E12.MirrorCS"),sQuery(id+"F0.wireOp",EDGE,"E14.MirrorCS"),sQuery(id+"F0.wireOp",EDGE,"E15.MirrorCS"),sQuery(id+"F0.wireOp",EDGE,"E16.MirrorCS"),sQuery(id+"F0.wireOp",EDGE,"E18.MirrorCS"),sQuery(id+"F0.wireOp",EDGE,"E19.MirrorCS"),sQuery(id+"F0.wireOp",EDGE,"E21.MirrorCS"),sQuery(id+"F0.wireOp",EDGE,"E24.MirrorCS"),sQuery(id+"F0.wireOp",EDGE,"E25.MirrorCS"),sQuery(id+"F0.wireOp",EDGE,"E26.MirrorCS"),sQuery(id+"F0.wireOp",EDGE,"E27.MirrorCS"),sQuery(id+"F0.wireOp",EDGE,"E28.MirrorCS"),sQuery(id+"F0.wireOp",EDGE,"E29.MirrorCS"),sQuery(id+"F0.wireOp",EDGE,"E30.MirrorCS"),sQuery(id+"F0.wireOp",EDGE,"E31.MirrorCS"),sQuery(id+"F0.wireOp",EDGE,"E32.MirrorCS"),sQuery(id+"F0.wireOp",EDGE,"E33.MirrorCS"),sQuery(id+"F0.wireOp",EDGE,"E34.MirrorCS"),sQuery(id+"F0.wireOp",EDGE,"E35.MirrorCS"),sQuery(id+"F0.wireOp",EDGE,"E38.MirrorCS"),sQuery(id+"F0.wireOp",EDGE,"E39.MirrorCS")])],"isStart":false}),"instanceName":"1"});
            var sketch = newSketch(context, id + "F28", { "sketchPlane" : qUnion([Q0])});
            skCircle(sketch, "E97.0", {"center": v(436.88, 92.08) * mm, "radius": 5.08 * mm});
            skCircle(sketch, "E98", {"center": v(436.88, 78.1) * mm, "radius": 19.05 * mm});
            skSolve(sketch);
        }
        {
            var Q0;
            Q0=makeQuery(id+"F28.imprint","IMPRINT",FACE,{"disambiguationData":[TD([[makeQuery(id+"F28.imprint","IMPRINT",EDGE,{"derivedFrom":sQuery(id+"F28.wireOp",EDGE,"E97.0")}),-1.0]])]});
            var Q1;
            Q1=makeQuery(id+"F28.imprint","IMPRINT",FACE,{"disambiguationData":[TD([[makeQuery(id+"F28.imprint","IMPRINT",EDGE,{"derivedFrom":sQuery(id+"F28.wireOp",EDGE,"E97.0")}),1.0]])]});
            extrude(context, id + "F29", {"entities" : qUnion([Q0, Q1]), "operationType" : NewBodyOperationType.REMOVE, "endBound" : BoundingType.THROUGH_ALL, "oppositeDirection" : true, "depth" : 25.4 * mm});
        }
        {
            var Q0;
            Q0=makeQuery(id+"F29.boolean.opBoolean","COPY",FACE,{"derivedFrom":makeQuery(id+"F29.opExtrude","SWEPT_FACE",FACE,{"disambiguationData":[OSD([sQuery(id+"F28.wireOp",EDGE,"E98")])]})});
            fillet(context, id + "F30", {"entities" : qUnion([Q0]), "radius" : 3.17 * mm, "tangentPropagation" : true, "allowEdgeOverflow" : false});
        }
        {
            var Q0;
            Q0=makeQuery(id+"F1.opExtrude","CAP_FACE",FACE,{"disambiguationData":[OSD([sQuery(id+"F0.wireOp",EDGE,"E0.bottom"),sQuery(id+"F0.wireOp",EDGE,"E0.top"),sQuery(id+"F0.wireOp",EDGE,"E0.left"),sQuery(id+"F0.wireOp",EDGE,"E1.top"),sQuery(id+"F0.wireOp",EDGE,"E1.right"),sQuery(id+"F0.wireOp",EDGE,"E2.0.1.1"),sQuery(id+"F0.wireOp",EDGE,"E2.0.1.2"),sQuery(id+"F0.wireOp",EDGE,"E2.0.1.3"),sQuery(id+"F0.wireOp",EDGE,"E2.0.2.1"),sQuery(id+"F0.wireOp",EDGE,"E2.0.2.2"),sQuery(id+"F0.wireOp",EDGE,"E2.0.2.3"),sQuery(id+"F0.wireOp",EDGE,"E2.0.3.1"),sQuery(id+"F0.wireOp",EDGE,"E2.0.3.2"),sQuery(id+"F0.wireOp",EDGE,"E2.0.3.3"),sQuery(id+"F0.wireOp",EDGE,"E2.0.4.1"),sQuery(id+"F0.wireOp",EDGE,"E2.0.4.2"),sQuery(id+"F0.wireOp",EDGE,"E2.0.4.3"),sQuery(id+"F0.wireOp",EDGE,"E2.0.5.1"),sQuery(id+"F0.wireOp",EDGE,"E2.0.5.2"),sQuery(id+"F0.wireOp",EDGE,"E2.0.5.3"),sQuery(id+"F0.wireOp",EDGE,"E2.0.6.1"),sQuery(id+"F0.wireOp",EDGE,"E2.0.6.2"),sQuery(id+"F0.wireOp",EDGE,"E2.0.6.3"),sQuery(id+"F0.wireOp",EDGE,"E2.0.7.1"),sQuery(id+"F0.wireOp",EDGE,"E2.0.7.2"),sQuery(id+"F0.wireOp",EDGE,"E2.0.7.3"),sQuery(id+"F0.wireOp",EDGE,"E5.MirrorCS"),sQuery(id+"F0.wireOp",EDGE,"E7.MirrorCS"),sQuery(id+"F0.wireOp",EDGE,"E8.MirrorCS"),sQuery(id+"F0.wireOp",EDGE,"E10.MirrorCS"),sQuery(id+"F0.wireOp",EDGE,"E11.MirrorCS"),sQuery(id+"F0.wireOp",EDGE,"E12.MirrorCS"),sQuery(id+"F0.wireOp",EDGE,"E14.MirrorCS"),sQuery(id+"F0.wireOp",EDGE,"E15.MirrorCS"),sQuery(id+"F0.wireOp",EDGE,"E16.MirrorCS"),sQuery(id+"F0.wireOp",EDGE,"E18.MirrorCS"),sQuery(id+"F0.wireOp",EDGE,"E19.MirrorCS"),sQuery(id+"F0.wireOp",EDGE,"E21.MirrorCS"),sQuery(id+"F0.wireOp",EDGE,"E24.MirrorCS"),sQuery(id+"F0.wireOp",EDGE,"E25.MirrorCS"),sQuery(id+"F0.wireOp",EDGE,"E26.MirrorCS"),sQuery(id+"F0.wireOp",EDGE,"E27.MirrorCS"),sQuery(id+"F0.wireOp",EDGE,"E28.MirrorCS"),sQuery(id+"F0.wireOp",EDGE,"E29.MirrorCS"),sQuery(id+"F0.wireOp",EDGE,"E30.MirrorCS"),sQuery(id+"F0.wireOp",EDGE,"E31.MirrorCS"),sQuery(id+"F0.wireOp",EDGE,"E32.MirrorCS"),sQuery(id+"F0.wireOp",EDGE,"E33.MirrorCS"),sQuery(id+"F0.wireOp",EDGE,"E34.MirrorCS"),sQuery(id+"F0.wireOp",EDGE,"E35.MirrorCS"),sQuery(id+"F0.wireOp",EDGE,"E38.MirrorCS"),sQuery(id+"F0.wireOp",EDGE,"E39.MirrorCS")])],"isStart":true});
            var sketch = newSketch(context, id + "F31", { "sketchPlane" : qUnion([Q0])});
            skCircle(sketch, "E99", {"center": v(-444.5, 63.5) * mm, "radius": 19.05 * mm});
            skLineSegment(sketch, "E100", {"start": v(-444.5, 63.5) * mm, "end": v(-444.5, 44.45) * mm, "construction": true});
            skCircle(sketch, "E101.MirrorC", {"center": v(444.5, 63.5) * mm, "radius": 19.05 * mm});
            skSolve(sketch);
        }
        {
            var Q0;
            Q0=makeQuery(id+"F31.imprint","IMPRINT",FACE,{"disambiguationData":[TD([[makeQuery(id+"F31.imprint","IMPRINT",EDGE,{"derivedFrom":sQuery(id+"F31.wireOp",EDGE,"E99")}),1.0]])]});
            var Q1;
            Q1=makeQuery(id+"F31.imprint","IMPRINT",FACE,{"disambiguationData":[TD([[makeQuery(id+"F31.imprint","IMPRINT",EDGE,{"derivedFrom":sQuery(id+"F31.wireOp",EDGE,"E101.MirrorC")}),-1.0]])]});
            var Q2;
            Q2=sQuery(id+"F31.wireOp",EDGE,"E99");
            var Q3;
            Q3=sQuery(id+"F31.wireOp",EDGE,"44c2cd6f-0501-4e53-9721-1fe3bb185338");
            var Q4;
            Q4=sQuery(id+"F31.wireOp",EDGE,"f3b6445c-b5e9-4b92-ba67-8c1365210f8b");
            var Q5;
            Q5=sQuery(id+"F31.wireOp",EDGE,"2c753216-6d3c-48c0-88b8-8c7134b6fa713.MirrorC");
            var Q6;
            Q6=sQuery(id+"F31.wireOp",EDGE,"2c753216-6d3c-48c0-88b8-8c7134b6fa716.MirrorC");
            var Q7;
            Q7=sQuery(id+"F31.wireOp",EDGE,"E101.MirrorC");
            extrude(context, id + "F32", {"entities" : qUnion([Q0, Q1]), "operationType" : NewBodyOperationType.REMOVE, "surfaceEntities" : qUnion([Q2, Q3, Q4, Q5, Q6, Q7]), "endBound" : BoundingType.THROUGH_ALL, "oppositeDirection" : true, "depth" : 25.4 * mm});
        }
        {
            var Q0;
            Q0=makeQuery(id+"F32.boolean.opBoolean","COPY",FACE,{"derivedFrom":makeQuery(id+"F32.opExtrude","SWEPT_FACE",FACE,{"disambiguationData":[OSD([sQuery(id+"F31.wireOp",EDGE,"E99")])]})});
            var Q1;
            Q1=makeQuery(id+"F32.boolean.opBoolean","COPY",FACE,{"derivedFrom":makeQuery(id+"F32.opExtrude","SWEPT_FACE",FACE,{"disambiguationData":[OSD([sQuery(id+"F31.wireOp",EDGE,"44c2cd6f-0501-4e53-9721-1fe3bb185338")])]})});
            var Q2;
            Q2=makeQuery(id+"F32.boolean.opBoolean","COPY",FACE,{"derivedFrom":makeQuery(id+"F32.opExtrude","SWEPT_FACE",FACE,{"disambiguationData":[OSD([sQuery(id+"F31.wireOp",EDGE,"f3b6445c-b5e9-4b92-ba67-8c1365210f8b")])]})});
            var Q3;
            Q3=makeQuery(id+"F32.boolean.opBoolean","COPY",FACE,{"derivedFrom":makeQuery(id+"F32.opExtrude","SWEPT_FACE",FACE,{"disambiguationData":[OSD([sQuery(id+"F31.wireOp",EDGE,"2c753216-6d3c-48c0-88b8-8c7134b6fa713.MirrorC")])]})});
            var Q4;
            Q4=makeQuery(id+"F32.boolean.opBoolean","COPY",FACE,{"derivedFrom":makeQuery(id+"F32.opExtrude","SWEPT_FACE",FACE,{"disambiguationData":[OSD([sQuery(id+"F31.wireOp",EDGE,"2c753216-6d3c-48c0-88b8-8c7134b6fa716.MirrorC")])]})});
            var Q5;
            Q5=makeQuery(id+"F32.boolean.opBoolean","COPY",FACE,{"derivedFrom":makeQuery(id+"F32.opExtrude","SWEPT_FACE",FACE,{"disambiguationData":[OSD([sQuery(id+"F31.wireOp",EDGE,"E101.MirrorC")])]})});
            fillet(context, id + "F33", {"entities" : qUnion([Q0, Q1, Q2, Q3, Q4, Q5]), "radius" : 3.17 * mm, "tangentPropagation" : true, "allowEdgeOverflow" : false});
        }
    });
